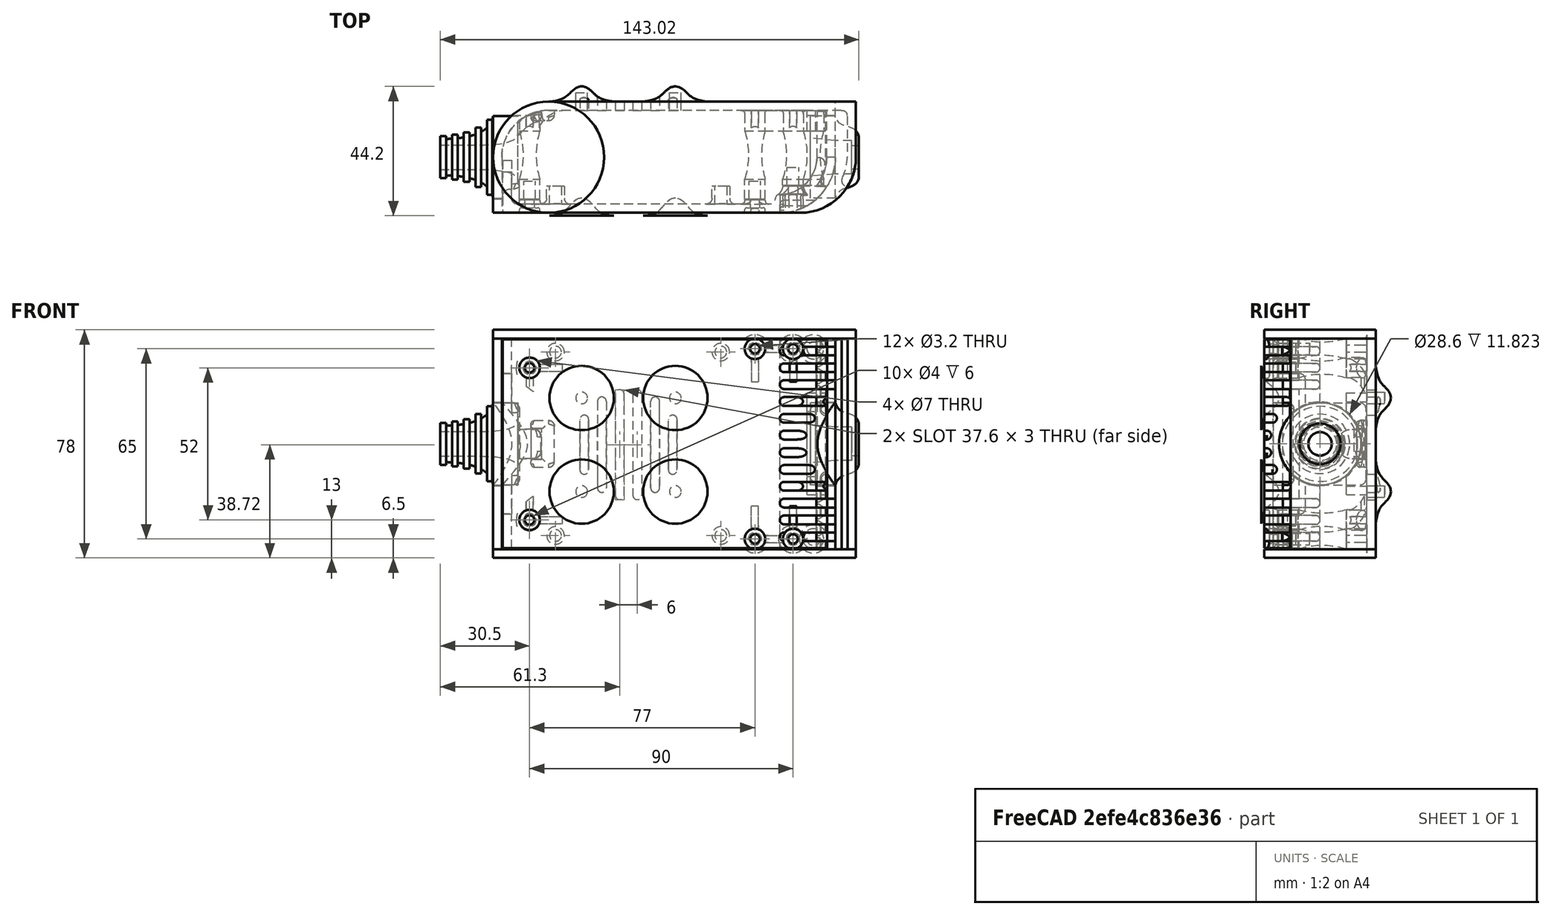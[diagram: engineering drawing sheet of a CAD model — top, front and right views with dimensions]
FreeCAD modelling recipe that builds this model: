
FCSTD DOCUMENT  (FreeCAD 0.19R0.19.2)
Label: enclosure_129
License: All rights reserved
LicenseURL: http://en.wikipedia.org/wiki/All_rights_reserved
objects: Part::Feature×74, Part::Revolution×74, Part::MultiFuse×61, Sketcher::SketchObject×38, Part::Fillet×27, Part::Extrusion×26, Part::Cut×25, Part::Cylinder×22, Part::Box×12, App::MeasureDistance×4
note: 359 computed .brp shape members not serialized (recipe doc carries the construction recipe); baked Part::Feature solids carry a one-line shape summary decoded from their .brp

FEATURE [Sketcher::SketchObject] Sketch  label="topSketch"
  FullyConstrained = true
  sketch-geometry (20):
    g0: LineSegment StartX=5.21097e-06 StartY=3 StartZ=0 EndX=5.21097e-06 EndY=19 EndZ=0
    g1: ArcOfCircle CenterX=19 CenterY=19 CenterZ=0 NormalX=0 NormalY=0 NormalZ=1 AngleXU=0 Radius=19 StartAngle=1.5708 EndAngle=3.14159
    g2: ArcOfCircle CenterX=19 CenterY=19 CenterZ=0 NormalX=0 NormalY=0 NormalZ=1 AngleXU=0 Radius=16 StartAngle=1.5708 EndAngle=3.14159
    g3: LineSegment StartX=114 StartY=35 StartZ=0 EndX=19 EndY=35 EndZ=0
    g4: LineSegment StartX=5.21097e-06 StartY=3 StartZ=0 EndX=5.21097e-06 EndY=0 EndZ=0
    g5: LineSegment StartX=3 StartY=0 StartZ=0 EndX=5.21097e-06 EndY=0 EndZ=0
    g6: LineSegment StartX=3 StartY=19 StartZ=0 EndX=3 EndY=0 EndZ=0
    g7: LineSegment StartX=19 StartY=38 StartZ=0 EndX=124 EndY=38 EndZ=0
    g8: Circle CenterX=119 CenterY=35 CenterZ=0 NormalX=0 NormalY=0 NormalZ=1 AngleXU=0 Radius=1
    g9: Circle CenterX=121 CenterY=35 CenterZ=0 NormalX=0 NormalY=0 NormalZ=1 AngleXU=0 Radius=1
    g10: Circle CenterX=121 CenterY=33 CenterZ=0 NormalX=0 NormalY=0 NormalZ=1 AngleXU=0 Radius=1
    g11: BSplineCurve PolesCount=3 KnotsCount=2 Degree=2 IsPeriodic=0
    g12: GeomPoint X=119 Y=35 Z=0
    g13: GeomPoint X=121 Y=33 Z=0
    g14: LineSegment StartX=119 StartY=35 StartZ=0 EndX=114 EndY=35 EndZ=0
    g15: ArcOfCircle CenterX=105 CenterY=19 CenterZ=0 NormalX=0 NormalY=0 NormalZ=1 AngleXU=0 Radius=19 StartAngle=5.7297 EndAngle=6.28319
    g16: ArcOfCircle CenterX=105 CenterY=19 CenterZ=0 NormalX=0 NormalY=0 NormalZ=1 AngleXU=0 Radius=16 StartAngle=5.60905 EndAngle=6.28319
    g17: LineSegment StartX=121 StartY=33 StartZ=0 EndX=121 EndY=19 EndZ=0
    g18: LineSegment StartX=124 StartY=38 StartZ=0 EndX=124 EndY=19 EndZ=0
    g19: LineSegment StartX=117.5 StartY=9.01251 StartZ=0 EndX=121.163 EndY=9.0125 EndZ=0
  constraints (46):
    c: Vertical(g0)
    c: Block(g0)
    c: Coincident(g1,g0)
    c: Block(g1)
    c: Coincident(g2,g1)
    c: Block(g2)
    c: Coincident(g3,g2)
    c: Horizontal(g3)
    c: Tangent(g3,g2)
    c: Coincident(g4,g0)
    c: Distance(g4) = 3
    c: Vertical(g4)
    c: Coincident(g5,g4)
    c: Horizontal(g5)
    c: Coincident(g6,g2)
    c: Coincident(g6,g5)
    c: Vertical(g6)
    c: Horizontal(g7)
    c: Distance(g7) = 105
    c: Coincident(g7,g1)
    c: Block(g3)
    c: Weight(g8) = 1
    c: Equal(g8,g9)
    c: Equal(g8,g10)
    c: InternalAlignment(g8,g11)
    c: InternalAlignment(g9,g11)
    c: InternalAlignment(g10,g11)
    c: InternalAlignment(g12,g11)
    c: InternalAlignment(g13,g11)
    c: Block(g11)
    c: Coincident(g14,g11)
    c: Coincident(g14,g3)
    c: Horizontal(g14)
    c: Block(g15)
    c: Coincident(g16,g15)
    c: Block(g16)
    c: Coincident(g17,g11)
    c: Coincident(g17,g16)
    c: Vertical(g17)
    c: Distance(g17) = 14
    c: Coincident(g18,g7)
    c: Coincident(g18,g15)
    c: Vertical(g18)
    c: Distance(g18) = 19
    c: Coincident(g19,g16)
    c: Coincident(g19,g15)
FEATURE [Sketcher::SketchObject] Sketch001  label="bottomSketch"
  FullyConstrained = true
  sketch-geometry (32):
    g0: LineSegment StartX=3.3 StartY=-6.03275e-07 StartZ=0 EndX=98 EndY=-6.03275e-07 EndZ=0
    g1: ArcOfCircle CenterX=98 CenterY=19 CenterZ=0 NormalX=0 NormalY=0 NormalZ=1 AngleXU=0 Radius=19 StartAngle=4.71239 EndAngle=5.71103
    g2: LineSegment StartX=6.3 StartY=8 StartZ=0 EndX=3.3 EndY=8 EndZ=0
    g3: LineSegment StartX=3.3 StartY=8 StartZ=0 EndX=3.3 EndY=-6.03275e-07 EndZ=0
    g4: ArcOfCircle CenterX=8.3 CenterY=5 CenterZ=0 NormalX=0 NormalY=0 NormalZ=1 AngleXU=0 Radius=2 StartAngle=3.14159 EndAngle=4.71239
    g5: LineSegment StartX=6.3 StartY=8 StartZ=0 EndX=6.3 EndY=5 EndZ=0
    g6: ArcOfCircle CenterX=98 CenterY=19 CenterZ=0 NormalX=0 NormalY=0 NormalZ=1 AngleXU=0 Radius=12.7 StartAngle=4.71239 EndAngle=6.28319
    g7: LineSegment StartX=94.7 StartY=3 StartZ=0 EndX=8.3 EndY=3 EndZ=0
    g8-g12: Circle x5 (B-spline internal-alignment scaffolding for g13; pole/knot coordinates omitted)
    g13: BSplineCurve PolesCount=5 KnotsCount=3 Degree=3 IsPeriodic=0
    g14: GeomPoint X=98 Y=6.3 Z=0
    g15: GeomPoint X=96.3938 Y=4.71946 Z=0
    g16: GeomPoint X=94.7 Y=3 Z=0
    g17-g23: Circle x7 (B-spline internal-alignment scaffolding for g24; pole/knot coordinates omitted)
    g24: BSplineCurve PolesCount=7 KnotsCount=5 Degree=3 IsPeriodic=0
    g25-g29: GeomPoint x5 (B-spline internal-alignment scaffolding for g24; pole/knot coordinates omitted)
    g30: ArcOfCircle CenterX=98 CenterY=19 CenterZ=0 NormalX=0 NormalY=0 NormalZ=1 AngleXU=0 Radius=15.7 StartAngle=5.81226 EndAngle=6.28319
    g31: LineSegment StartX=110.7 StartY=19 StartZ=0 EndX=113.7 EndY=19 EndZ=0
  constraints (41):
    c: Horizontal(g0)
    c: Coincident(g1,g0)
    c: Block(g1)
    c: Horizontal(g2)
    c: Distance(g2) = 3
    c: Coincident(g3,g2)
    c: Vertical(g3)
    c: Coincident(g3,g0)
    c: Block(g4)
    c: Block(g2)
    c: Coincident(g5,g2)
    c: Coincident(g5,g4)
    c: Vertical(g5)
    c: Coincident(g6,g1)
    c: Block(g6)
    c: Coincident(g7,g4)
    c: Horizontal(g7)
    c: Block(g0)
    c: Block(g7)
    c: Block(g3)
    c: Coincident(g13,g6)
    c: Weight(g8) = 1
    c: Equal(g8, g9-g12) x4
    c: Coincident(g13,g7)
    c: InternalAlignment(g8-g12 -> g13) x5
    c: InternalAlignment(g14,g13)
    c: InternalAlignment(g15,g13)
    c: InternalAlignment(g16,g13)
    c: Block(g13)
    c: Weight(g17) = 1
    c: Equal(g17, g18-g23) x6
    c: Coincident(g24,g1)
    c: InternalAlignment(g17-g23 -> g24) x7
    c: InternalAlignment(g25-g29 -> g24) x5
    c: Block(g24)
    c: Coincident(g30,g24)
    c: Coincident(g31,g6)
    c: Coincident(g31,g30)
    c: Horizontal(g31)
    c: Block(g31)
    c: Block(g30)
FEATURE [Part::Extrusion] Extrude  label="top"
  Base = -> Sketch
  Dir = (0,0,1)
  DirMode = 2
  FaceMakerClass = Part::FaceMakerBullseye
  LengthFwd = 72
  LengthRev = 0
  Solid = true
  Symmetric = false
FEATURE [Part::Extrusion] Extrude001  label="bottom"
  Base = -> Sketch001
  Dir = (0,0,1)
  DirMode = 2
  FaceMakerClass = Part::FaceMakerBullseye
  LengthFwd = 71.4
  LengthRev = 0
  Placement = pos=(0,0,0.3) rot=(0,0,1;0rad)
  Solid = true
  Symmetric = false
FEATURE [Sketcher::SketchObject] Sketch002  label="topSketch001"
  FullyConstrained = true
  sketch-geometry (6):
    g0: ArcOfCircle CenterX=19 CenterY=19 CenterZ=0 NormalX=0 NormalY=0 NormalZ=1 AngleXU=0 Radius=19 StartAngle=1.5708 EndAngle=3.14159
    g1: LineSegment StartX=5.22862e-06 StartY=19 StartZ=0 EndX=5.22862e-06 EndY=1.19904e-11 EndZ=0
    g2: LineSegment StartX=19 StartY=38 StartZ=0 EndX=124 EndY=38 EndZ=0
    g3: LineSegment StartX=5.22862e-06 StartY=1.19904e-11 StartZ=0 EndX=105 EndY=1.19904e-11 EndZ=0
    g4: ArcOfCircle CenterX=105 CenterY=19 CenterZ=0 NormalX=0 NormalY=0 NormalZ=1 AngleXU=0 Radius=19 StartAngle=4.71239 EndAngle=6.28319
    g5: LineSegment StartX=124 StartY=38 StartZ=0 EndX=124 EndY=19 EndZ=0
  constraints (16):
    c: Block(g0)
    c: Coincident(g1,g0)
    c: Vertical(g1)
    c: Horizontal(g2)
    c: Distance(g2) = 105
    c: Coincident(g2,g0)
    c: Distance(g1) = 19
    c: Coincident(g3,g1)
    c: Horizontal(g3)
    c: Distance(g3) = 105
    c: Block(g4)
    c: Coincident(g4,g3)
    c: Coincident(g5,g2)
    c: Coincident(g5,g4)
    c: Vertical(g5)
    c: Distance(g5) = 19
FEATURE [Part::Extrusion] Extrude002  label="sideA"
  Base = -> Sketch002
  Dir = (0,0,1)
  DirMode = 2
  FaceMakerClass = Part::FaceMakerBullseye
  LengthFwd = 3
  LengthRev = 0
  Placement = pos=(0,0,-3) rot=(0,0,1;0rad)
  Solid = true
  Symmetric = false
FEATURE [Sketcher::SketchObject] Sketch003  label="topSketch002"
  FullyConstrained = true
  sketch-geometry (6):
    g0: LineSegment StartX=19 StartY=38 StartZ=0 EndX=117 EndY=38 EndZ=0
    g1: ArcOfCircle CenterX=19 CenterY=19 CenterZ=0 NormalX=0 NormalY=0 NormalZ=1 AngleXU=0 Radius=19 StartAngle=1.5708 EndAngle=3.14159
    g2: LineSegment StartX=117 StartY=38 StartZ=0 EndX=117 EndY=19 EndZ=0
    g3: LineSegment StartX=98 StartY=1.0161e-12 StartZ=0 EndX=5.22862e-06 EndY=1.0161e-12 EndZ=0
    g4: LineSegment StartX=5.22862e-06 StartY=19 StartZ=0 EndX=5.22862e-06 EndY=1.0161e-12 EndZ=0
    g5: ArcOfCircle CenterX=98 CenterY=19 CenterZ=0 NormalX=0 NormalY=0 NormalZ=1 AngleXU=0 Radius=19 StartAngle=4.71239 EndAngle=6.28319
  constraints (16):
    c: Horizontal(g0)
    c: Distance(g0) = 98
    c: Coincident(g1,g0)
    c: Block(g1)
    c: Coincident(g2,g0)
    c: Vertical(g2)
    c: Distance(g2) = 19
    c: Horizontal(g3)
    c: Coincident(g4,g1)
    c: Vertical(g4)
    c: Coincident(g3,g4)
    c: Block(g3)
    c: Coincident(g5,g2)
    c: Coincident(g5,g3)
    c: Block(g0)
    c: Block(g5)
FEATURE [Sketcher::SketchObject] Sketch004
  FullyConstrained = true
  MapMode = 3
  Placement = pos=(0,0,0) rot=(1,0,0;1.5708rad)
  Support = -> [Extrude]
  sketch-geometry (8):
    g0: Circle CenterX=80.351 CenterY=-67.6202 CenterZ=0 NormalX=0 NormalY=0 NormalZ=1 AngleXU=0 Radius=2
    g1: Circle CenterX=80.351 CenterY=-67.6202 CenterZ=0 NormalX=0 NormalY=0 NormalZ=1 AngleXU=0 Radius=3
    g2: Circle CenterX=80.351 CenterY=-4.92017 CenterZ=0 NormalX=0 NormalY=0 NormalZ=1 AngleXU=0 Radius=2
    g3: Circle CenterX=80.351 CenterY=-4.92017 CenterZ=0 NormalX=0 NormalY=0 NormalZ=1 AngleXU=0 Radius=3
    g4: Circle CenterX=23.851 CenterY=-4.92017 CenterZ=0 NormalX=0 NormalY=0 NormalZ=1 AngleXU=0 Radius=2
    g5: Circle CenterX=23.851 CenterY=-4.92017 CenterZ=0 NormalX=0 NormalY=0 NormalZ=1 AngleXU=0 Radius=3
    g6: Circle CenterX=23.851 CenterY=-67.6202 CenterZ=0 NormalX=0 NormalY=0 NormalZ=1 AngleXU=0 Radius=2
    g7: Circle CenterX=23.851 CenterY=-67.6202 CenterZ=0 NormalX=0 NormalY=0 NormalZ=1 AngleXU=0 Radius=3
  constraints (8):
    c: Block(g3)
    c: Block(g2)
    c: Block(g1)
    c: Block(g0)
    c: Block(g6)
    c: Block(g7)
    c: Block(g4)
    c: Block(g5)
FEATURE [Part::Extrusion] Extrude004
  Base = -> Sketch004
  Dir = (0,-1,2e-16)
  DirMode = 2
  FaceMakerClass = Part::FaceMakerBullseye
  LengthFwd = 6
  LengthRev = 0
  Placement = pos=(0,9,0) rot=(0,0,1;0rad)
  Solid = true
  Symmetric = false
FEATURE [Sketcher::SketchObject] Sketch005
  FullyConstrained = true
  MapMode = 3
  Placement = pos=(0,0,0) rot=(1,0,0;1.5708rad)
  Support = -> [Extrude]
  sketch-geometry (8):
    g0: Circle CenterX=80.351 CenterY=-67.6202 CenterZ=0 NormalX=0 NormalY=0 NormalZ=1 AngleXU=0 Radius=3
    g1: Circle CenterX=80.351 CenterY=-4.92017 CenterZ=0 NormalX=0 NormalY=0 NormalZ=1 AngleXU=0 Radius=3
    g2: Circle CenterX=23.851 CenterY=-4.92017 CenterZ=0 NormalX=0 NormalY=0 NormalZ=1 AngleXU=0 Radius=3
    g3: Circle CenterX=23.851 CenterY=-67.6202 CenterZ=0 NormalX=0 NormalY=0 NormalZ=1 AngleXU=0 Radius=3
    g4: Circle CenterX=23.851 CenterY=-67.6202 CenterZ=0 NormalX=0 NormalY=0 NormalZ=1 AngleXU=0 Radius=5
    g5: Circle CenterX=80.351 CenterY=-67.6202 CenterZ=0 NormalX=0 NormalY=0 NormalZ=1 AngleXU=0 Radius=5
    g6: Circle CenterX=23.851 CenterY=-4.92017 CenterZ=0 NormalX=0 NormalY=0 NormalZ=1 AngleXU=0 Radius=5
    g7: Circle CenterX=80.351 CenterY=-4.92017 CenterZ=0 NormalX=0 NormalY=0 NormalZ=1 AngleXU=0 Radius=5
  constraints (8):
    c: Block(g1)
    c: Block(g0)
    c: Block(g3)
    c: Block(g2)
    c: Block(g5)
    c: Block(g4)
    c: Block(g6)
    c: Block(g7)
FEATURE [Part::Extrusion] Extrude005
  Base = -> Sketch005
  Dir = (0,-1,2e-16)
  DirMode = 2
  FaceMakerClass = Part::FaceMakerBullseye
  LengthFwd = 2
  LengthRev = 0
  Solid = true
  Symmetric = false
FEATURE [Sketcher::SketchObject] Sketch006
  FullyConstrained = true
  MapMode = 3
  Placement = pos=(0,0,0) rot=(1,0,0;1.5708rad)
  sketch-geometry (8):
    g0: Circle CenterX=80.351 CenterY=-67.6202 CenterZ=0 NormalX=0 NormalY=0 NormalZ=1 AngleXU=0 Radius=3
    g1: Circle CenterX=80.351 CenterY=-4.92017 CenterZ=0 NormalX=0 NormalY=0 NormalZ=1 AngleXU=0 Radius=3
    g2: Circle CenterX=23.851 CenterY=-4.92017 CenterZ=0 NormalX=0 NormalY=0 NormalZ=1 AngleXU=0 Radius=3
    g3: Circle CenterX=23.851 CenterY=-67.6202 CenterZ=0 NormalX=0 NormalY=0 NormalZ=1 AngleXU=0 Radius=3
    g4: Circle CenterX=23.851 CenterY=-67.6202 CenterZ=0 NormalX=0 NormalY=0 NormalZ=1 AngleXU=0 Radius=5
    g5: Circle CenterX=80.351 CenterY=-67.6202 CenterZ=0 NormalX=0 NormalY=0 NormalZ=1 AngleXU=0 Radius=5
    g6: Circle CenterX=23.851 CenterY=-4.92017 CenterZ=0 NormalX=0 NormalY=0 NormalZ=1 AngleXU=0 Radius=5
    g7: Circle CenterX=80.351 CenterY=-4.92017 CenterZ=0 NormalX=0 NormalY=0 NormalZ=1 AngleXU=0 Radius=5
  constraints (8):
    c: Block(g1)
    c: Block(g0)
    c: Block(g3)
    c: Block(g2)
    c: Block(g5)
    c: Block(g4)
    c: Block(g6)
    c: Block(g7)
FEATURE [Part::Extrusion] Extrude007
  Base = -> Sketch006
  Dir = (0,-1,2e-16)
  DirMode = 2
  FaceMakerClass = Part::FaceMakerBullseye
  LengthFwd = 2
  LengthRev = 0
  Solid = true
  Symmetric = false
FEATURE [Part::Fillet] Fillet
  Base = -> Extrude007
  Edges = 4 edges r=1.99: [Edge6,Edge12,Edge18,Edge24]
FEATURE [Part::Cut] Cut
  Base = -> Extrude005
  Placement = pos=(0,5,0) rot=(0,0,1;0rad)
  Tool = -> Fillet
FEATURE [Part::MultiFuse] Fusion  label="pCBScrews"
  Placement = pos=(-2.5,0,72.3) rot=(0,0,1;0rad)
  Shapes = -> [Extrude004,Cut]
FEATURE [App::MeasureDistance] Distance  label="Distance: 0.69 mm"
  Distance = 0.685967
  P1 = (24.0138,2.9647,0.3)
  P2 = (23.8901,3,-0.373787)
FEATURE [App::MeasureDistance] Distance001  label="Distance: 0.53 mm"
  Distance = 0.533607
  P1 = (80.2939,3,72.2334)
  P2 = (80.281,2.99661,71.7)
FEATURE [Part::Fillet] Fillet001
  Base = -> Extrude001
  Edges = 1 edges r=2.4: [Edge17]
FEATURE [Part::Fillet] Fillet002  label="bottom001"
  Base = -> Fillet001
  Edges = 1 edges r=2.4: [Edge36]
FEATURE [Part::Fillet] Fillet003  label="top001"
  Base = -> Extrude
  Edges = 1 edges r=2: [Edge1]
FEATURE [Sketcher::SketchObject] Sketch007
  FullyConstrained = true
  sketch-geometry (16):
    g0: LineSegment StartX=4 StartY=0 StartZ=0 EndX=4 EndY=2.4 EndZ=0
    g1: LineSegment StartX=4 StartY=2.4 StartZ=0 EndX=7 EndY=2.4 EndZ=0
    g2: LineSegment StartX=4 StartY=0 StartZ=0 EndX=5.7 EndY=0 EndZ=0
    g3: LineSegment StartX=5.7 StartY=0 StartZ=0 EndX=5.7 EndY=-5.6 EndZ=0
    g4-g8: Circle x5 (B-spline internal-alignment scaffolding for g9; pole/knot coordinates omitted)
    g9: BSplineCurve PolesCount=5 KnotsCount=3 Degree=3 IsPeriodic=0
    g10: GeomPoint X=7 Y=2.4 Z=0
    g11: GeomPoint X=10.4582 Y=-1.55472 Z=0
    g12: GeomPoint X=14 Y=-5.6 Z=0
    g13: LineSegment StartX=14 StartY=-5.6 StartZ=0 EndX=14 EndY=-14.1 EndZ=0
    g14: LineSegment StartX=14 StartY=-14.1 StartZ=0 EndX=6.5 EndY=-14.1 EndZ=0
    g15: LineSegment StartX=5.7 StartY=-5.6 StartZ=0 EndX=6.5 EndY=-14.1 EndZ=0
  constraints (28):
    c: Distance(g0) = 2.4
    c: Vertical(g0)
    c: Block(g0)
    c: Coincident(g1,g0)
    c: Horizontal(g1)
    c: Distance(g1) = 3
    c: Coincident(g2,g0)
    c: Horizontal(g2)
    c: Distance(g2) = 1.7
    c: Coincident(g3,g2)
    c: Vertical(g3)
    c: Distance(g3) = 5.6
    c: Coincident(g9,g1)
    c: Weight(g4) = 1
    c: Equal(g4, g5-g8) x4
    c: InternalAlignment(g4-g8 -> g9) x5
    c: InternalAlignment(g10,g9)
    c: InternalAlignment(g11,g9)
    c: InternalAlignment(g12,g9)
    c: Block(g9)
    c: Coincident(g13,g9)
    c: Vertical(g13)
    c: Distance(g13) = 8.5
    c: Coincident(g14,g13)
    c: Horizontal(g14)
    c: Distance(g14) = 7.5
    c: Coincident(g15,g3)
    c: Coincident(g15,g14)
FEATURE [Part::Feature] Face
  shape: bbox 10 x 16.5 x 2e-07 mm, 1 faces, 0 solids (baked)
FEATURE [Part::Revolution] Revolve  label="plugHousing"
  Angle = 360
  Axis = (0,1,0)
  Base = (0,0,0)
  FaceMakerClass = Part::FaceMakerBullseye
  Placement = pos=(0,0,36.15) rot=(0,0,1;0rad)
  Solid = false
  Source = -> Face
  Symmetric = false
FEATURE [Part::Feature] Face001
  shape: bbox 10 x 16.5 x 2e-07 mm, 1 faces, 0 solids (baked)
FEATURE [Part::Revolution] Revolve001  label="plugHousing001"
  Angle = 360
  Axis = (0,1,0)
  Base = (0,0,0)
  FaceMakerClass = Part::FaceMakerBullseye
  Placement = pos=(0,0,36.15) rot=(0,0,1;0rad)
  Solid = false
  Source = -> Face001
  Symmetric = false
FEATURE [Part::MultiFuse] Fusion001  label="plugHousing002"
  Placement = pos=(0,0,0) rot=(0,0,1;1.5708rad)
  Shapes = -> [Revolve001,Revolve]
FEATURE [Part::Feature] Face002
  shape: bbox 10 x 16.5 x 2e-07 mm, 1 faces, 0 solids (baked)
FEATURE [Part::Revolution] Revolve003  label="plugHousing005"
  Angle = 360
  Axis = (0,1,0)
  Base = (0,0,0)
  FaceMakerClass = Part::FaceMakerBullseye
  Placement = pos=(0,0,36.15) rot=(0,0,1;0rad)
  Solid = false
  Source = -> Face002
  Symmetric = false
FEATURE [Part::Feature] Face003
  shape: bbox 10 x 16.5 x 2e-07 mm, 1 faces, 0 solids (baked)
FEATURE [Part::Revolution] Revolve002  label="plugHousing003"
  Angle = 360
  Axis = (0,1,0)
  Base = (0,0,0)
  FaceMakerClass = Part::FaceMakerBullseye
  Placement = pos=(0,0,36.15) rot=(0,0,1;0rad)
  Solid = false
  Source = -> Face003
  Symmetric = false
FEATURE [Part::MultiFuse] Fusion002  label="plugHousing004"
  Placement = pos=(0,0,0) rot=(0,0,1;1.5708rad)
  Shapes = -> [Revolve002,Revolve003]
FEATURE [Part::MultiFuse] Fusion003  label="plugHousing006"
  Placement = pos=(0,19,0) rot=(0,0,1;3.14159rad)
  Shapes = -> [Fusion002,Fusion001]
FEATURE [Part::Feature] Face004
  shape: bbox 10 x 16.5 x 2e-07 mm, 1 faces, 0 solids (baked)
FEATURE [Part::Revolution] Revolve006  label="plugHousing010"
  Angle = 360
  Axis = (0,1,0)
  Base = (0,0,0)
  FaceMakerClass = Part::FaceMakerBullseye
  Placement = pos=(0,0,36.15) rot=(0,0,1;0rad)
  Solid = false
  Source = -> Face004
  Symmetric = false
FEATURE [Part::Feature] Face005
  shape: bbox 10 x 16.5 x 2e-07 mm, 1 faces, 0 solids (baked)
FEATURE [Part::Revolution] Revolve007  label="plugHousing011"
  Angle = 360
  Axis = (0,1,0)
  Base = (0,0,0)
  FaceMakerClass = Part::FaceMakerBullseye
  Placement = pos=(0,0,36.15) rot=(0,0,1;0rad)
  Solid = false
  Source = -> Face005
  Symmetric = false
FEATURE [Part::Feature] Face006
  shape: bbox 10 x 16.5 x 2e-07 mm, 1 faces, 0 solids (baked)
FEATURE [Part::Revolution] Revolve004  label="plugHousing007"
  Angle = 360
  Axis = (0,1,0)
  Base = (0,0,0)
  FaceMakerClass = Part::FaceMakerBullseye
  Placement = pos=(0,0,36.15) rot=(0,0,1;0rad)
  Solid = false
  Source = -> Face006
  Symmetric = false
FEATURE [Part::MultiFuse] Fusion004  label="plugHousing009"
  Placement = pos=(0,0,0) rot=(0,0,1;1.5708rad)
  Shapes = -> [Revolve004,Revolve007]
FEATURE [Part::Feature] Face007
  shape: bbox 10 x 16.5 x 2e-07 mm, 1 faces, 0 solids (baked)
FEATURE [Part::Revolution] Revolve005  label="plugHousing008"
  Angle = 360
  Axis = (0,1,0)
  Base = (0,0,0)
  FaceMakerClass = Part::FaceMakerBullseye
  Placement = pos=(0,0,36.15) rot=(0,0,1;0rad)
  Solid = false
  Source = -> Face007
  Symmetric = false
FEATURE [Part::MultiFuse] Fusion005  label="plugHousing012"
  Placement = pos=(0,0,0) rot=(0,0,1;1.5708rad)
  Shapes = -> [Revolve006,Revolve005]
FEATURE [Part::MultiFuse] Fusion006  label="plugHousing013"
  Placement = pos=(0,19,0) rot=(0,0,1;3.14159rad)
  Shapes = -> [Fusion005,Fusion004]
FEATURE [Part::MultiFuse] Fusion007  label="plugHousing014"
  Placement = pos=(122.621,0,-0.15) rot=(0,0,1;0rad)
  Shapes = -> [Fusion003,Fusion006]
FEATURE [Part::Cylinder] Cylinder002
  Angle = 360
  AttacherType = Attacher::AttachEngine3D
  Height = 20
  Placement = pos=(0,0,36.15) rot=(0,0,1;0rad)
  Radius = 4
FEATURE [Part::Cylinder] Cylinder003
  Angle = 360
  AttacherType = Attacher::AttachEngine3D
  Height = 10
  Placement = pos=(0,0,36.15) rot=(0,0,1;0rad)
  Radius = 4
FEATURE [Part::MultiFuse] Fusion009  label="removeToCreateHoleForPlugHousing"
  Placement = pos=(70,19,36.15) rot=(0,1,0;1.5708rad)
  Shapes = -> [Cylinder002,Cylinder003]
FEATURE [Part::Cylinder] Cylinder004
  Angle = 360
  AttacherType = Attacher::AttachEngine3D
  Height = 20
  Placement = pos=(0,0,36.15) rot=(0,0,1;0rad)
  Radius = 4
FEATURE [Part::Cylinder] Cylinder005
  Angle = 360
  AttacherType = Attacher::AttachEngine3D
  Height = 10
  Placement = pos=(0,0,36.15) rot=(0,0,1;0rad)
  Radius = 4
FEATURE [Part::MultiFuse] Fusion010  label="removeToCreateHoleForPlugHousing001"
  Placement = pos=(70,19,36.15) rot=(0,1,0;1.5708rad)
  Shapes = -> [Cylinder004,Cylinder005]
FEATURE [Part::Cut] Cut001
  Base = -> Fillet003
  Tool = -> Fusion010
FEATURE [Part::Cut] Cut002  label="Bottom"
  Base = -> Fillet002
  Tool = -> Fusion009
FEATURE [Part::Feature] Face008
  shape: bbox 10 x 16.5 x 2e-07 mm, 1 faces, 0 solids (baked)
FEATURE [Part::Revolution] Revolve011  label="plugHousing021"
  Angle = 360
  Axis = (0,1,0)
  Base = (0,0,0)
  FaceMakerClass = Part::FaceMakerBullseye
  Placement = pos=(0,0,36.15) rot=(0,0,1;0rad)
  Solid = false
  Source = -> Face008
  Symmetric = false
FEATURE [Part::Feature] Face009
  shape: bbox 10 x 16.5 x 2e-07 mm, 1 faces, 0 solids (baked)
FEATURE [Part::Revolution] Revolve012  label="plugHousing022"
  Angle = 360
  Axis = (0,1,0)
  Base = (0,0,0)
  FaceMakerClass = Part::FaceMakerBullseye
  Placement = pos=(0,0,36.15) rot=(0,0,1;0rad)
  Solid = false
  Source = -> Face009
  Symmetric = false
FEATURE [Part::Feature] Face010 .. Face013  x4 (patterned run collapsed; names and placements below)
  shape: bbox 10 x 16.5 x 2e-07 mm, 1 faces, 0 solids (baked)
FEATURE [Part::Revolution] Revolve015  label="plugHousing027"
  Angle = 360
  Axis = (0,1,0)
  Base = (0,0,0)
  FaceMakerClass = Part::FaceMakerBullseye
  Placement = pos=(0,0,36.15) rot=(0,0,1;0rad)
  Solid = false
  Source = -> Face013
  Symmetric = false
FEATURE [Part::Feature] Face014
  shape: bbox 10 x 16.5 x 2e-07 mm, 1 faces, 0 solids (baked)
FEATURE [Part::Feature] Face015
  shape: bbox 10 x 16.5 x 2e-07 mm, 1 faces, 0 solids (baked)
FEATURE [Part::Feature] Face016
  shape: bbox 10 x 16.5 x 2e-07 mm, 1 faces, 0 solids (baked)
FEATURE [Part::Revolution] Revolve019  label="plugHousing033"
  Angle = 360
  Axis = (0,1,0)
  Base = (0,0,0)
  FaceMakerClass = Part::FaceMakerBullseye
  Placement = pos=(0,0,36.15) rot=(0,0,1;0rad)
  Solid = false
  Source = -> Face016
  Symmetric = false
FEATURE [Part::Feature] Face017
  shape: bbox 10 x 16.5 x 2e-07 mm, 1 faces, 0 solids (baked)
FEATURE [Part::Revolution] Revolve020  label="plugHousing034"
  Angle = 360
  Axis = (0,1,0)
  Base = (0,0,0)
  FaceMakerClass = Part::FaceMakerBullseye
  Placement = pos=(0,0,36.15) rot=(0,0,1;0rad)
  Solid = false
  Source = -> Face017
  Symmetric = false
FEATURE [Part::Feature] Face018
  shape: bbox 10 x 16.5 x 2e-07 mm, 1 faces, 0 solids (baked)
FEATURE [Part::Revolution] Revolve016  label="plugHousing030"
  Angle = 360
  Axis = (0,1,0)
  Base = (0,0,0)
  FaceMakerClass = Part::FaceMakerBullseye
  Placement = pos=(0,0,36.15) rot=(0,0,1;0rad)
  Solid = false
  Source = -> Face018
  Symmetric = false
FEATURE [Part::MultiFuse] Fusion020  label="plugHousing038"
  Placement = pos=(0,0,0) rot=(0,0,1;1.5708rad)
  Shapes = -> [Revolve016,Revolve020]
FEATURE [Part::Feature] Face019
  shape: bbox 10 x 16.5 x 2e-07 mm, 1 faces, 0 solids (baked)
FEATURE [Part::Feature] Face020
  shape: bbox 10 x 16.5 x 2e-07 mm, 1 faces, 0 solids (baked)
FEATURE [Part::Revolution] Revolve017  label="plugHousing031"
  Angle = 360
  Axis = (0,1,0)
  Base = (0,0,0)
  FaceMakerClass = Part::FaceMakerBullseye
  Placement = pos=(0,0,36.15) rot=(0,0,1;0rad)
  Solid = false
  Source = -> Face020
  Symmetric = false
FEATURE [Part::MultiFuse] Fusion021  label="plugHousing039"
  Placement = pos=(0,0,0) rot=(0,0,1;1.5708rad)
  Shapes = -> [Revolve019,Revolve017]
FEATURE [Part::MultiFuse] Fusion023  label="plugHousing041"
  Placement = pos=(0,19,0) rot=(0,0,1;3.14159rad)
  Shapes = -> [Fusion021,Fusion020]
FEATURE [Part::Revolution] Revolve022  label="plugHousing043"
  Angle = 360
  Axis = (0,1,0)
  Base = (0,0,0)
  FaceMakerClass = Part::FaceMakerBullseye
  Placement = pos=(0,0,36.15) rot=(0,0,1;0rad)
  Solid = false
  Source = -> Face019
  Symmetric = false
FEATURE [Part::Feature] Face021
  shape: bbox 10 x 16.5 x 2e-07 mm, 1 faces, 0 solids (baked)
FEATURE [Part::Revolution] Revolve023  label="plugHousing044"
  Angle = 360
  Axis = (0,1,0)
  Base = (0,0,0)
  FaceMakerClass = Part::FaceMakerBullseye
  Placement = pos=(0,0,36.15) rot=(0,0,1;0rad)
  Solid = false
  Source = -> Face021
  Symmetric = false
FEATURE [Part::Feature] Face022
  shape: bbox 10 x 16.5 x 2e-07 mm, 1 faces, 0 solids (baked)
FEATURE [Part::Revolution] Revolve018  label="plugHousing032"
  Angle = 360
  Axis = (0,1,0)
  Base = (0,0,0)
  FaceMakerClass = Part::FaceMakerBullseye
  Placement = pos=(0,0,36.15) rot=(0,0,1;0rad)
  Solid = false
  Source = -> Face022
  Symmetric = false
FEATURE [Part::MultiFuse] Fusion022  label="plugHousing040"
  Placement = pos=(0,0,0) rot=(0,0,1;1.5708rad)
  Shapes = -> [Revolve018,Revolve023]
FEATURE [Part::Feature] Face023
  shape: bbox 10 x 16.5 x 2e-07 mm, 1 faces, 0 solids (baked)
FEATURE [Part::Revolution] Revolve021  label="plugHousing035"
  Angle = 360
  Axis = (0,1,0)
  Base = (0,0,0)
  FaceMakerClass = Part::FaceMakerBullseye
  Placement = pos=(0,0,36.15) rot=(0,0,1;0rad)
  Solid = false
  Source = -> Face023
  Symmetric = false
FEATURE [Part::MultiFuse] Fusion018  label="plugHousing036"
  Placement = pos=(0,0,0) rot=(0,0,1;1.5708rad)
  Shapes = -> [Revolve022,Revolve021]
FEATURE [Part::MultiFuse] Fusion019  label="plugHousing037"
  Placement = pos=(0,19,0) rot=(0,0,1;3.14159rad)
  Shapes = -> [Fusion018,Fusion022]
FEATURE [Part::MultiFuse] Fusion024  label="plugHousing042"
  Placement = pos=(122.621,0,-0.15) rot=(0,0,1;0rad)
  Shapes = -> [Fusion023,Fusion019]
FEATURE [Part::Cylinder] Cylinder006
  Angle = 360
  AttacherType = Attacher::AttachEngine3D
  Height = 20
  Placement = pos=(0,0,36.15) rot=(0,0,1;0rad)
  Radius = 14.3
FEATURE [Part::Cylinder] Cylinder007
  Angle = 360
  AttacherType = Attacher::AttachEngine3D
  Height = 10
  Placement = pos=(0,0,36.15) rot=(0,0,1;0rad)
  Radius = 4
FEATURE [Part::MultiFuse] Fusion026  label="removeToCreteHoleForPlugHousing"
  Placement = pos=(70,19,36) rot=(0,1,0;1.5708rad)
  Shapes = -> [Cylinder006,Cylinder007]
FEATURE [Part::Box] Box001  label="Cube001"
  AttacherType = Attacher::AttachEngine3D
  Height = 28
  Length = 3
  Placement = pos=(110.7,19,22) rot=(0,0,1;0rad)
  Width = 15.7
FEATURE [Part::Cut] Cut003  label="top002"
  Base = -> Cut001
  Tool = -> Fusion007
FEATURE [Part::Revolution] Revolve008  label="plugHousing015"
  Angle = 360
  Axis = (0,1,0)
  Base = (0,0,0)
  FaceMakerClass = Part::FaceMakerBullseye
  Placement = pos=(0,0,36.15) rot=(0,0,1;0rad)
  Solid = false
  Source = -> Face010
  Symmetric = false
FEATURE [Part::MultiFuse] Fusion013  label="plugHousing020"
  Placement = pos=(0,0,0) rot=(0,0,1;1.5708rad)
  Shapes = -> [Revolve008,Revolve012]
FEATURE [Part::Cut] Cut004  label="top003"
  Base = -> Cut003
  Placement = pos=(1,0,0) rot=(0,0,1;0rad)
  Tool = -> Fusion026
FEATURE [Part::Cylinder] Cylinder008
  Angle = 360
  AttacherType = Attacher::AttachEngine3D
  Height = 20
  Placement = pos=(0,0,36.15) rot=(0,0,1;0rad)
  Radius = 10.3
FEATURE [Part::Cylinder] Cylinder009
  Angle = 360
  AttacherType = Attacher::AttachEngine3D
  Height = 10
  Placement = pos=(0,0,36.15) rot=(0,0,1;0rad)
  Radius = 4
FEATURE [Part::MultiFuse] Fusion027  label="removeToCreteHoleForPlugHousing001"
  Placement = pos=(70,19,36) rot=(0,1,0;1.5708rad)
  Shapes = -> [Cylinder008,Cylinder009]
FEATURE [Part::Cut] Cut005  label="plugHousingTab"
  Base = -> Box001
  Tool = -> Fusion027
FEATURE [Part::MultiFuse] Fusion028  label="plugHousing045"
  Shapes = -> [Fusion024,Cut005]
FEATURE [Part::Box] Box002  label="Cube002"
  AttacherType = Attacher::AttachEngine3D
  Height = 28.8
  Length = 3
  Placement = pos=(107.3,28,21.6) rot=(0,0,1;0rad)
  Width = 7
FEATURE [Part::Box] Box003  label="Cube003"
  AttacherType = Attacher::AttachEngine3D
  Height = 3
  Length = 6.4
  Placement = pos=(107.3,28,18.6) rot=(0,0,1;0rad)
  Width = 7
FEATURE [Part::Box] Box004  label="Cube004"
  AttacherType = Attacher::AttachEngine3D
  Height = 3
  Length = 6.4
  Placement = pos=(107.3,28,50.4) rot=(0,0,1;0rad)
  Width = 7
FEATURE [Part::MultiFuse] Fusion029  label="plugHousingBracketHolder"
  Shapes = -> [Box004,Box002,Box003]
FEATURE [Part::Cylinder] Cylinder010
  Angle = 360
  AttacherType = Attacher::AttachEngine3D
  Height = 20
  Placement = pos=(0,0,36.15) rot=(0,0,1;0rad)
  Radius = 14.3
FEATURE [Part::Cylinder] Cylinder011
  Angle = 360
  AttacherType = Attacher::AttachEngine3D
  Height = 10
  Placement = pos=(0,0,36.15) rot=(0,0,1;0rad)
  Radius = 4
FEATURE [Part::MultiFuse] Fusion030  label="removeToCreteHoleForPlugHousing002"
  Placement = pos=(70,19,36) rot=(0,1,0;1.5708rad)
  Shapes = -> [Cylinder010,Cylinder011]
FEATURE [Part::Cut] Cut006  label="plugHousingBracketHolder001"
  Base = -> Fusion029
  Tool = -> Fusion030
FEATURE [Part::Cylinder] Cylinder012
  Angle = 360
  AttacherType = Attacher::AttachEngine3D
  Height = 20
  Placement = pos=(0,0,36.15) rot=(0,0,1;0rad)
  Radius = 7
FEATURE [Part::Cylinder] Cylinder013
  Angle = 360
  AttacherType = Attacher::AttachEngine3D
  Height = 10
  Placement = pos=(0,0,36.15) rot=(0,0,1;0rad)
  Radius = 4
FEATURE [Part::MultiFuse] Fusion032  label="removeToCreteHoleForPlugHousing003"
  Placement = pos=(70,19,36) rot=(0,1,0;1.5708rad)
  Shapes = -> [Cylinder012,Cylinder013]
FEATURE [Part::Cut] Cut007  label="bottom002"
  Base = -> Cut002
  Tool = -> Fusion032
FEATURE [Sketcher::SketchObject] Sketch008
  FullyConstrained = true
  sketch-geometry (54):
    g0: LineSegment StartX=-4.2 StartY=0 StartZ=0 EndX=-6.2 EndY=0 EndZ=0
    g1: LineSegment StartX=-14 StartY=-18 StartZ=0 EndX=-14 EndY=-26.5 EndZ=0
    g2: LineSegment StartX=-4.2 StartY=0 StartZ=0 EndX=-4.2 EndY=-13.4877 EndZ=0
    g3: Circle CenterX=-4.2 CenterY=-13.4877 CenterZ=0 NormalX=0 NormalY=0 NormalZ=1 AngleXU=0 Radius=1
    g4: Circle CenterX=-4.2 CenterY=-26.5 CenterZ=0 NormalX=0 NormalY=0 NormalZ=1 AngleXU=0 Radius=1
    g5: Circle CenterX=-8.2 CenterY=-26.5 CenterZ=0 NormalX=0 NormalY=0 NormalZ=1 AngleXU=0 Radius=1
    g6: BSplineCurve PolesCount=3 KnotsCount=2 Degree=2 IsPeriodic=0
    g7: GeomPoint X=-4.2 Y=-13.4877 Z=0
    g8: GeomPoint X=-8.2 Y=-26.5 Z=0
    g9: LineSegment StartX=-14 StartY=-26.5 StartZ=0 EndX=-8.2 EndY=-26.5 EndZ=0
    g10: LineSegment StartX=-10.15 StartY=-12 StartZ=0 EndX=-10.15 EndY=-14 EndZ=0
    g11: LineSegment StartX=-12.8401 StartY=-16 StartZ=0 EndX=-10.1571 EndY=-16 EndZ=0
    g12: LineSegment StartX=-10.15 StartY=-14 StartZ=0 EndX=-8.70761 EndY=-14 EndZ=0
    g13: LineSegment StartX=-12.8401 StartY=-16 StartZ=0 EndX=-12.8401 EndY=-17.6958 EndZ=0
    g14: LineSegment StartX=-10.15 StartY=-12 StartZ=0 EndX=-7.79258 EndY=-12 EndZ=0
    g15: Circle CenterX=-6.2215 CenterY=-2 CenterZ=0 NormalX=0 NormalY=0 NormalZ=1 AngleXU=0 Radius=1
    g16: Circle CenterX=-6.22762 CenterY=-2.58724 CenterZ=0 NormalX=0 NormalY=0 NormalZ=1 AngleXU=0 Radius=1
    g17: Circle CenterX=-6.32538 CenterY=-4 CenterZ=0 NormalX=0 NormalY=0 NormalZ=1 AngleXU=0 Radius=1
    g18: BSplineCurve PolesCount=3 KnotsCount=2 Degree=2 IsPeriodic=0
    g19: GeomPoint X=-6.2215 Y=-2 Z=0
    g20: GeomPoint X=-6.32538 Y=-4 Z=0
    g21: Circle CenterX=-6.48644 CenterY=-5.99526 CenterZ=0 NormalX=0 NormalY=0 NormalZ=1 AngleXU=0 Radius=1
    g22: Circle CenterX=-6.58486 CenterY=-6.99526 CenterZ=0 NormalX=0 NormalY=0 NormalZ=1 AngleXU=0 Radius=1
    g23: Circle CenterX=-6.77343 CenterY=-8 CenterZ=0 NormalX=0 NormalY=0 NormalZ=1 AngleXU=0 Radius=1
    g24: BSplineCurve PolesCount=3 KnotsCount=2 Degree=2 IsPeriodic=0
    g25: GeomPoint X=-6.48644 Y=-5.99526 Z=0
    g26: GeomPoint X=-6.77343 Y=-8 Z=0
    g27: Circle CenterX=-7.19003 CenterY=-10 CenterZ=0 NormalX=0 NormalY=0 NormalZ=1 AngleXU=0 Radius=1
    g28: Circle CenterX=-7.44407 CenterY=-11.0915 CenterZ=0 NormalX=0 NormalY=0 NormalZ=1 AngleXU=0 Radius=1
    g29: Circle CenterX=-7.79258 CenterY=-12 CenterZ=0 NormalX=0 NormalY=0 NormalZ=1 AngleXU=0 Radius=1
    g30: BSplineCurve PolesCount=3 KnotsCount=2 Degree=2 IsPeriodic=0
    g31: GeomPoint X=-7.19003 Y=-10 Z=0
    g32: GeomPoint X=-7.79258 Y=-12 Z=0
    g33: Circle CenterX=-8.70761 CenterY=-14 CenterZ=0 NormalX=0 NormalY=0 NormalZ=1 AngleXU=0 Radius=1
    g34: Circle CenterX=-9.33087 CenterY=-15.1837 CenterZ=0 NormalX=0 NormalY=0 NormalZ=1 AngleXU=0 Radius=1
    g35: Circle CenterX=-10.1571 CenterY=-16 CenterZ=0 NormalX=0 NormalY=0 NormalZ=1 AngleXU=0 Radius=1
    g36: BSplineCurve PolesCount=3 KnotsCount=2 Degree=2 IsPeriodic=0
    g37: GeomPoint X=-8.70761 Y=-14 Z=0
    g38: GeomPoint X=-10.1571 Y=-16 Z=0
    g39: Circle CenterX=-12.8401 CenterY=-17.6958 CenterZ=0 NormalX=0 NormalY=0 NormalZ=1 AngleXU=0 Radius=1
    g40: Circle CenterX=-13.3521 CenterY=-17.9027 CenterZ=0 NormalX=0 NormalY=0 NormalZ=1 AngleXU=0 Radius=1
    g41: Circle CenterX=-14 CenterY=-18 CenterZ=0 NormalX=0 NormalY=0 NormalZ=1 AngleXU=0 Radius=1
    g42: BSplineCurve PolesCount=3 KnotsCount=2 Degree=2 IsPeriodic=0
    g43: GeomPoint X=-12.8401 Y=-17.6958 Z=0
    g44: GeomPoint X=-14 Y=-18 Z=0
    g45: LineSegment StartX=-6.2 StartY=0 StartZ=0 EndX=-7.2 EndY=0 EndZ=0
    g46: LineSegment StartX=-7.2 StartY=0 StartZ=0 EndX=-7.2 EndY=-2 EndZ=0
    g47: LineSegment StartX=-7.2 StartY=-2 StartZ=0 EndX=-6.2215 EndY=-2 EndZ=0
    g48: LineSegment StartX=-6.32538 StartY=-4 StartZ=0 EndX=-7.65538 EndY=-4 EndZ=0
    g49: LineSegment StartX=-7.65538 StartY=-4 StartZ=0 EndX=-7.65538 EndY=-5.99526 EndZ=0
    g50: LineSegment StartX=-7.65538 StartY=-5.99526 StartZ=0 EndX=-6.48644 EndY=-5.99526 EndZ=0
    g51: LineSegment StartX=-6.77343 StartY=-8 StartZ=0 EndX=-8.43343 EndY=-8 EndZ=0
    g52: LineSegment StartX=-8.43343 StartY=-8 StartZ=0 EndX=-8.43343 EndY=-10 EndZ=0
    g53: LineSegment StartX=-8.43343 StartY=-10 StartZ=0 EndX=-7.19003 EndY=-10 EndZ=0
  constraints (112):
    c: Horizontal(g0)
    c: Distance(g0) = 2
    c: Block(g0)
    c: Vertical(g1)
    c: Coincident(g2,g0)
    c: Vertical(g2)
    c: Block(g2)
    c: Coincident(g6,g2)
    c: Weight(g3) = 1
    c: Equal(g3,g4)
    c: Equal(g3,g5)
    c: InternalAlignment(g3,g6)
    c: InternalAlignment(g4,g6)
    c: InternalAlignment(g5,g6)
    c: InternalAlignment(g7,g6)
    c: InternalAlignment(g8,g6)
    c: Block(g6)
    c: Coincident(g9,g1)
    c: Coincident(g9,g6)
    c: Horizontal(g9)
    c: Vertical(g10)
    c: Block(g10)
    c: Horizontal(g11)
    c: Block(g11)
    c: Coincident(g12,g10)
    c: Horizontal(g12)
    c: Block(g12)
    c: Coincident(g13,g11)
    c: Vertical(g13)
    c: Block(g13)
    c: Coincident(g14,g10)
    c: Horizontal(g14)
    c: Block(g14)
    c: Block(g9)
    c: Block(g1)
    c: Weight(g15) = 1
    c: Equal(g15,g16)
    c: Equal(g15,g17)
    c: InternalAlignment(g15,g18)
    c: InternalAlignment(g16,g18)
    c: InternalAlignment(g17,g18)
    c: InternalAlignment(g19,g18)
    c: InternalAlignment(g20,g18)
    c: Weight(g21) = 1
    c: Equal(g21,g22)
    c: Equal(g21,g23)
    c: InternalAlignment(g21,g24)
    c: InternalAlignment(g22,g24)
    c: InternalAlignment(g23,g24)
    c: InternalAlignment(g25,g24)
    c: InternalAlignment(g26,g24)
    c: Weight(g27) = 1
    c: Equal(g27,g28)
    c: Equal(g27,g29)
    c: Coincident(g30,g14)
    c: InternalAlignment(g27,g30)
    c: InternalAlignment(g28,g30)
    c: InternalAlignment(g29,g30)
    c: InternalAlignment(g31,g30)
    c: InternalAlignment(g32,g30)
    c: Coincident(g36,g12)
    c: Weight(g33) = 1
    c: Equal(g33,g34)
    c: Equal(g33,g35)
    c: Coincident(g36,g11)
    c: InternalAlignment(g33,g36)
    c: InternalAlignment(g34,g36)
    c: InternalAlignment(g35,g36)
    c: InternalAlignment(g37,g36)
    c: InternalAlignment(g38,g36)
    c: Coincident(g42,g13)
    c: Weight(g39) = 1
    c: Equal(g39,g40)
    c: Equal(g39,g41)
    c: Coincident(g42,g1)
    c: InternalAlignment(g39,g42)
    c: InternalAlignment(g40,g42)
    c: InternalAlignment(g41,g42)
    c: InternalAlignment(g43,g42)
    c: InternalAlignment(g44,g42)
    c: Block(g18)
    c: Block(g24)
    c: Block(g30)
    c: Block(g36)
    c: Block(g42)
    c: Horizontal(g45)
    c: Coincident(g45,g0)
    c: Vertical(g46)
    c: Coincident(g46,g45)
    c: Coincident(g47,g46)
    c: Coincident(g47,g18)
    c: Horizontal(g47)
    c: Block(g46)
    c: Coincident(g48,g18)
    c: Horizontal(g48)
    c: Distance(g48) = 1.33
    c: Vertical(g49)
    c: Coincident(g49,g48)
    c: Coincident(g50,g49)
    c: Coincident(g50,g24)
    c: Horizontal(g50)
    c: Tangent(g50,g22)
    c: Horizontal(g51)
    c: Coincident(g51,g24)
    c: Block(g51)
    c: Vertical(g52)
    c: Block(g52)
    c: Coincident(g52,g51)
    c: Coincident(g53,g52)
    c: Coincident(g53,g30)
    c: Horizontal(g53)
    c: Distance(g1) = 8.5
FEATURE [Part::Feature] Face024
  shape: bbox 9.8 x 26.5 x 2e-07 mm, 1 faces, 0 solids (baked)
FEATURE [Part::Revolution] Revolve024
  Angle = 360
  Axis = (0,1,0)
  Base = (0,0,0)
  FaceMakerClass = Part::FaceMakerBullseye
  Placement = pos=(0,0,0) rot=(0,0,1;1.5708rad)
  Solid = false
  Source = -> Face024
  Symmetric = false
FEATURE [Part::Feature] Face025
  shape: bbox 9.8 x 26.5 x 2e-07 mm, 1 faces, 0 solids (baked)
FEATURE [Part::Revolution] Revolve025
  Angle = 360
  Axis = (0,1,0)
  Base = (0,0,0)
  FaceMakerClass = Part::FaceMakerBullseye
  Placement = pos=(0,0,0) rot=(0,0,1;1.5708rad)
  Solid = false
  Source = -> Face025
  Symmetric = false
FEATURE [Part::MultiFuse] Fusion033
  Placement = pos=(-18,19,36) rot=(0,0,1;0rad)
  Shapes = -> [Revolve025,Revolve024]
FEATURE [Part::Cylinder] Cylinder014
  Angle = 360
  AttacherType = Attacher::AttachEngine3D
  Height = 20
  Placement = pos=(0,0,36.15) rot=(0,0,1;0rad)
  Radius = 14.3
FEATURE [Part::Cylinder] Cylinder015
  Angle = 360
  AttacherType = Attacher::AttachEngine3D
  Height = 10
  Placement = pos=(0,0,36.15) rot=(0,0,1;0rad)
  Radius = 4
FEATURE [Part::MultiFuse] Fusion034  label="removeToCreteHoleForPlugHousing004"
  Placement = pos=(-42,19,36) rot=(0,1,0;1.5708rad)
  Shapes = -> [Cylinder014,Cylinder015]
FEATURE [Part::Cut] Cut008  label="top004"
  Base = -> Cut004
  Placement = pos=(-1,0,0) rot=(0,0,1;0rad)
  Tool = -> Fusion034
FEATURE [Part::Box] Box005  label="Cube005"
  AttacherType = Attacher::AttachEngine3D
  Height = 28
  Length = 3
  Placement = pos=(110.7,19,22) rot=(0,0,1;0rad)
  Width = 15.7
FEATURE [Part::Cylinder] Cylinder016
  Angle = 360
  AttacherType = Attacher::AttachEngine3D
  Height = 10
  Placement = pos=(0,0,36.15) rot=(0,0,1;0rad)
  Radius = 4
FEATURE [Part::Cylinder] Cylinder017
  Angle = 360
  AttacherType = Attacher::AttachEngine3D
  Height = 20
  Placement = pos=(0,0,36.15) rot=(0,0,1;0rad)
  Radius = 10.3
FEATURE [Part::MultiFuse] Fusion035  label="removeToCreteHoleForPlugHousing005"
  Placement = pos=(70,19,36) rot=(0,1,0;1.5708rad)
  Shapes = -> [Cylinder017,Cylinder016]
FEATURE [Part::Cut] Cut009  label="plugHousingTab001"
  Base = -> Box005
  Placement = pos=(-107.4,-14,0) rot=(0,0,1;0rad)
  Tool = -> Fusion035
FEATURE [Part::Box] Box006  label="Cube006"
  AttacherType = Attacher::AttachEngine3D
  Height = 28
  Length = 3
  Placement = pos=(110.7,19,22) rot=(0,0,1;0rad)
  Width = 15.7
FEATURE [Part::Cylinder] Cylinder018
  Angle = 360
  AttacherType = Attacher::AttachEngine3D
  Height = 10
  Placement = pos=(0,0,36.15) rot=(0,0,1;0rad)
  Radius = 4
FEATURE [Part::Cylinder] Cylinder019
  Angle = 360
  AttacherType = Attacher::AttachEngine3D
  Height = 20
  Placement = pos=(0,0,36.15) rot=(0,0,1;0rad)
  Radius = 10.3
FEATURE [Part::MultiFuse] Fusion036  label="removeToCreteHoleForPlugHousing006"
  Placement = pos=(70,19,36) rot=(0,1,0;1.5708rad)
  Shapes = -> [Cylinder019,Cylinder018]
FEATURE [Part::Cut] Cut010  label="plugHousingTab002"
  Base = -> Box006
  Placement = pos=(-107.4,-14,0) rot=(0,0,1;0rad)
  Tool = -> Fusion036
FEATURE [Part::MultiFuse] Fusion037
  Placement = pos=(9.6,23,0) rot=(0,0,1;3.14159rad)
  Shapes = -> [Cut009,Cut010]
FEATURE [Part::Box] Box  label="Cube"
  AttacherType = Attacher::AttachEngine3D
  Height = 10
  Length = 3
  Placement = pos=(3.3,4,12) rot=(0,0,1;0rad)
  Width = 10
FEATURE [Part::Fillet] Fillet004
  Base = -> Fusion028
  Edges = 1 edges r=2: [Edge25]
FEATURE [Part::Fillet] Fillet005  label="plugHousing046"
  Base = -> Fillet004
  Edges = 1 edges r=2: [Edge8]
FEATURE [Part::Fillet] Fillet006
  Base = -> Box
  Edges = 1 edges r=2: [Edge11]
FEATURE [Part::Box] Box007  label="Cube007"
  AttacherType = Attacher::AttachEngine3D
  Height = 10
  Length = 3
  Placement = pos=(3.3,4,50) rot=(0,0,1;0rad)
  Width = 10
FEATURE [Part::Fillet] Fillet007
  Base = -> Box007
  Edges = 1 edges r=2: [Edge12]
FEATURE [Part::Box] Box008  label="Cube008"
  AttacherType = Attacher::AttachEngine3D
  Height = 28
  Length = 4
  Placement = pos=(5,0,22) rot=(0,0,1;0rad)
  Width = 10
FEATURE [Part::Fillet] Fillet008
  Base = -> Box008
  Edges = 1 edges r=1: [Edge7]
FEATURE [Part::Fillet] Fillet009
  Base = -> Fillet008
  Edges = 1 edges r=2: [Edge5]
FEATURE [Part::Fillet] Fillet010
  Base = -> Fillet009
  Edges = 1 edges r=2: [Edge2]
FEATURE [Sketcher::SketchObject] Sketch009  label="topSketch003"
  FullyConstrained = true
  sketch-geometry (4):
    g0: LineSegment StartX=16.8446 StartY=31.512 StartZ=0 EndX=16.3251 EndY=34.4666 EndZ=0
    g1: ArcOfCircle CenterX=19 CenterY=19.2524 CenterZ=0 NormalX=0 NormalY=0 NormalZ=1 AngleXU=0 Radius=15.4476 StartAngle=1.74483 EndAngle=2.72717
    g2: ArcOfCircle CenterX=19 CenterY=19.2524 CenterZ=0 NormalX=0 NormalY=0 NormalZ=1 AngleXU=0 Radius=12.4476 StartAngle=1.74483 EndAngle=2.73189
    g3: LineSegment StartX=4.86004 StartY=25.4725 StartZ=0 EndX=7.58253 EndY=24.2107 EndZ=0
  constraints (7):
    c: Block(g0)
    c: Coincident(g1,g0)
    c: Coincident(g2,g0)
    c: Coincident(g3,g1)
    c: Coincident(g3,g2)
    c: Block(g1)
    c: Block(g2)
FEATURE [Part::Extrusion] Extrude008
  Base = -> Sketch009
  Dir = (0,0,1)
  DirMode = 2
  FaceMakerClass = Part::FaceMakerBullseye
  LengthFwd = 10
  LengthRev = 0
  Placement = pos=(0,0,31) rot=(0,0,1;0rad)
  Solid = true
  Symmetric = false
FEATURE [Part::Cylinder] Cylinder020
  Angle = 360
  AttacherType = Attacher::AttachEngine3D
  Height = 20
  Placement = pos=(0,0,36.15) rot=(0,0,1;0rad)
  Radius = 8.2
FEATURE [Part::Cylinder] Cylinder021
  Angle = 360
  AttacherType = Attacher::AttachEngine3D
  Height = 10
  Placement = pos=(0,0,36.15) rot=(0,0,1;0rad)
  Radius = 4
FEATURE [Part::MultiFuse] Fusion038  label="removeToCreteHoleForPlugHousing007"
  Placement = pos=(-42,19,36) rot=(0,1,0;1.5708rad)
  Shapes = -> [Cylinder020,Cylinder021]
FEATURE [Part::Cut] Cut011
  Base = -> Extrude008
  Tool = -> Fusion038
FEATURE [Part::Fillet] Fillet011
  Base = -> Cut011
  Edges = 1 edges r=2: [Edge1]
FEATURE [Part::Fillet] Fillet012
  Base = -> Fillet011
  Edges = 1 edges r=2.5: [Edge1]
FEATURE [Part::Fillet] Fillet013
  Base = -> Fillet012
  Edges = 1 edges r=2.5: [Edge2]
FEATURE [Part::Box] Box010  label="Cube010"
  AttacherType = Attacher::AttachEngine3D
  Height = 16
  Length = 8
  Placement = pos=(12.7,31.52,28) rot=(0,0,1;0rad)
  Width = 4
FEATURE [Sketcher::SketchObject] Sketch010  label="topSketch004"
  FullyConstrained = true
  sketch-geometry (4):
    g0: LineSegment StartX=16.8446 StartY=31.512 StartZ=0 EndX=16.3251 EndY=34.4666 EndZ=0
    g1: ArcOfCircle CenterX=19 CenterY=19.2524 CenterZ=0 NormalX=0 NormalY=0 NormalZ=1 AngleXU=0 Radius=15.4476 StartAngle=1.74483 EndAngle=2.72717
    g2: ArcOfCircle CenterX=19 CenterY=19.2524 CenterZ=0 NormalX=0 NormalY=0 NormalZ=1 AngleXU=0 Radius=12.4476 StartAngle=1.74483 EndAngle=2.73189
    g3: LineSegment StartX=4.86004 StartY=25.4725 StartZ=0 EndX=7.58253 EndY=24.2107 EndZ=0
  constraints (7):
    c: Block(g0)
    c: Coincident(g1,g0)
    c: Coincident(g2,g0)
    c: Coincident(g3,g1)
    c: Coincident(g3,g2)
    c: Block(g1)
    c: Block(g2)
FEATURE [Part::Cylinder] Cylinder022
  Angle = 360
  AttacherType = Attacher::AttachEngine3D
  Height = 10
  Placement = pos=(0,0,36.15) rot=(0,0,1;0rad)
  Radius = 4
FEATURE [Sketcher::SketchObject] Sketch011  label="topSketch005"
  FullyConstrained = true
  sketch-geometry (4):
    g0: LineSegment StartX=16.8446 StartY=31.512 StartZ=0 EndX=16.3251 EndY=34.4666 EndZ=0
    g1: ArcOfCircle CenterX=19 CenterY=19.2524 CenterZ=0 NormalX=0 NormalY=0 NormalZ=1 AngleXU=0 Radius=15.4476 StartAngle=1.74483 EndAngle=2.72717
    g2: ArcOfCircle CenterX=19 CenterY=19.2524 CenterZ=0 NormalX=0 NormalY=0 NormalZ=1 AngleXU=0 Radius=12.4476 StartAngle=1.74483 EndAngle=2.73189
    g3: LineSegment StartX=4.86004 StartY=25.4725 StartZ=0 EndX=7.58253 EndY=24.2107 EndZ=0
  constraints (7):
    c: Block(g0)
    c: Coincident(g1,g0)
    c: Coincident(g2,g0)
    c: Coincident(g3,g1)
    c: Coincident(g3,g2)
    c: Block(g1)
    c: Block(g2)
FEATURE [Part::Extrusion] Extrude010
  Base = -> Sketch011
  Dir = (0,0,1)
  DirMode = 2
  FaceMakerClass = Part::FaceMakerBullseye
  LengthFwd = 10.6
  LengthRev = 0
  Placement = pos=(0,0,31) rot=(0,0,1;0rad)
  Solid = true
  Symmetric = false
FEATURE [Part::Cylinder] Cylinder023
  Angle = 360
  AttacherType = Attacher::AttachEngine3D
  Height = 20
  Placement = pos=(0,0,36.15) rot=(0,0,1;0rad)
  Radius = 8.2
FEATURE [Part::MultiFuse] Fusion039  label="removeToCreteHoleForPlugHousing008"
  Placement = pos=(-42,19,36) rot=(0,1,0;1.5708rad)
  Shapes = -> [Cylinder023,Cylinder022]
FEATURE [Part::Cut] Cut012
  Base = -> Extrude010
  Placement = pos=(0,0,-0.3) rot=(0,0,1;0rad)
  Tool = -> Fusion039
FEATURE [Part::Cut] Cut013
  Base = -> Box010
  Tool = -> Cut012
FEATURE [Part::Fillet] Fillet014
  Base = -> Cut013
  Edges = 1 edges r=0.7: [Edge13]
FEATURE [Part::Fillet] Fillet015
  Base = -> Fillet014
  Edges = 1 edges r=0.7: [Edge13]
FEATURE [Part::Fillet] Fillet016
  Base = -> Fillet015
  Edges = 1 edges r=0.7: [Edge16]
FEATURE [Part::Fillet] Fillet017
  Base = -> Fillet016
  Edges = 1 edges r=0.7: [Edge11]
FEATURE [Part::Fillet] Fillet018
  Base = -> Fillet017
  Edges = 1 edges r=0.7: [Edge10]
FEATURE [Part::Fillet] Fillet019
  Base = -> Fillet018
  Edges = 1 edges r=1.2: [Edge5]
FEATURE [Part::Fillet] Fillet020
  Base = -> Fillet019
  Edges = 1 edges r=1.2: [Edge12]
FEATURE [Part::Fillet] Fillet021
  Base = -> Fillet020
  Edges = 1 edges r=2: [Edge1]
  Placement = pos=(0.3,0,0) rot=(0,0,1;0rad)
FEATURE [Part::MultiFuse] Fusion040  label="top005"
  Shapes = -> [Cut008,Fillet021]
FEATURE [Part::MultiFuse] Fusion041  label="wireHolder"
  Shapes = -> [Fusion033,Fillet013]
FEATURE [Part::MultiFuse] Fusion042
  Shapes = -> [Fillet007,Fusion041]
FEATURE [Part::MultiFuse] Fusion043  label="wireHolder001"
  Shapes = -> [Fusion042,Fillet010]
FEATURE [Part::MultiFuse] Fusion044  label="wireHolder002"
  Shapes = -> [Fillet006,Fusion037,Fusion043]
FEATURE [Part::Feature] Face026
  shape: bbox 11 x 6 x 2e-07 mm, 1 faces, 0 solids (baked)
FEATURE [Part::Revolution] Revolve026
  Angle = 360
  Axis = (0,1,0)
  Base = (0,0,0)
  FaceMakerClass = Part::FaceMakerBullseye
  Placement = pos=(30.3,-1,19.7) rot=(0,0,1;0rad)
  Solid = false
  Source = -> Face026
  Symmetric = false
FEATURE [Sketcher::SketchObject] Sketch013  label="topSketch006"
  FullyConstrained = true
  sketch-geometry (13):
    g0: LineSegment StartX=117 StartY=19 StartZ=0 EndX=117 EndY=38 EndZ=0
    g1: ArcOfCircle CenterX=98 CenterY=19 CenterZ=0 NormalX=0 NormalY=0 NormalZ=1 AngleXU=0 Radius=19 StartAngle=5.7297 EndAngle=6.28319
    g2: LineSegment StartX=0 StartY=3 StartZ=0 EndX=0 EndY=19 EndZ=0
    g3: LineSegment StartX=19 StartY=38 StartZ=0 EndX=117 EndY=38 EndZ=0
    g4: ArcOfCircle CenterX=19 CenterY=19 CenterZ=0 NormalX=0 NormalY=0 NormalZ=1 AngleXU=0 Radius=19 StartAngle=1.5708 EndAngle=3.14159
    g5: ArcOfCircle CenterX=19 CenterY=19 CenterZ=0 NormalX=0 NormalY=0 NormalZ=1 AngleXU=0 Radius=16 StartAngle=1.5708 EndAngle=3.14159
    g6: ArcOfCircle CenterX=98 CenterY=19 CenterZ=0 NormalX=0 NormalY=0 NormalZ=1 AngleXU=0 Radius=16 StartAngle=5.60905 EndAngle=6.28319
    g7: LineSegment StartX=114 StartY=19 StartZ=0 EndX=114 EndY=35 EndZ=0
    g8: LineSegment StartX=110.5 StartY=9.01251 StartZ=0 EndX=114.163 EndY=9.01251 EndZ=0
    g9: LineSegment StartX=114 StartY=35 StartZ=0 EndX=19 EndY=35 EndZ=0
    g10: LineSegment StartX=0 StartY=3 StartZ=0 EndX=0 EndY=0 EndZ=0
    g11: LineSegment StartX=3 StartY=0 StartZ=0 EndX=0 EndY=0 EndZ=0
    g12: LineSegment StartX=3 StartY=19 StartZ=0 EndX=3 EndY=0 EndZ=0
  constraints (33):
    c: Vertical(g0)
    c: Distance(g0) = 19
    c: Block(g0)
    c: Coincident(g1,g0)
    c: Block(g1)
    c: Vertical(g2)
    c: Block(g2)
    c: Coincident(g3,g0)
    c: Horizontal(g3)
    c: Distance(g3) = 98
    c: Coincident(g4,g3)
    c: Coincident(g4,g2)
    c: Block(g4)
    c: Coincident(g5,g4)
    c: Coincident(g6,g1)
    c: Block(g6)
    c: Block(g5)
    c: Coincident(g7,g6)
    c: Vertical(g7)
    c: Coincident(g8,g6)
    c: Coincident(g8,g1)
    c: Coincident(g9,g7)
    c: Coincident(g9,g5)
    c: Horizontal(g9)
    c: Tangent(g9,g5)
    c: Coincident(g10,g2)
    c: Distance(g10) = 3
    c: Vertical(g10)
    c: Coincident(g11,g10)
    c: Horizontal(g11)
    c: Coincident(g12,g5)
    c: Coincident(g12,g11)
    c: Vertical(g12)
FEATURE [Part::Extrusion] Extrude011  label="top006"
  Base = -> Sketch013
  Dir = (0,0,1)
  DirMode = 2
  FaceMakerClass = Part::FaceMakerBullseye
  LengthFwd = 72
  LengthRev = 0
  Solid = true
  Symmetric = false
FEATURE [Sketcher::SketchObject] Sketch014
  FullyConstrained = true
  MapMode = 3
  Placement = pos=(0,0,0) rot=(1,0,0;1.5708rad)
  Support = -> [Extrude011]
  sketch-geometry (8):
    g0: Circle CenterX=80.351 CenterY=-67.6202 CenterZ=0 NormalX=0 NormalY=0 NormalZ=1 AngleXU=0 Radius=2
    g1: Circle CenterX=80.351 CenterY=-67.6202 CenterZ=0 NormalX=0 NormalY=0 NormalZ=1 AngleXU=0 Radius=3
    g2: Circle CenterX=80.351 CenterY=-4.92017 CenterZ=0 NormalX=0 NormalY=0 NormalZ=1 AngleXU=0 Radius=2
    g3: Circle CenterX=80.351 CenterY=-4.92017 CenterZ=0 NormalX=0 NormalY=0 NormalZ=1 AngleXU=0 Radius=3
    g4: Circle CenterX=23.851 CenterY=-4.92017 CenterZ=0 NormalX=0 NormalY=0 NormalZ=1 AngleXU=0 Radius=2
    g5: Circle CenterX=23.851 CenterY=-4.92017 CenterZ=0 NormalX=0 NormalY=0 NormalZ=1 AngleXU=0 Radius=3
    g6: Circle CenterX=23.851 CenterY=-67.6202 CenterZ=0 NormalX=0 NormalY=0 NormalZ=1 AngleXU=0 Radius=2
    g7: Circle CenterX=23.851 CenterY=-67.6202 CenterZ=0 NormalX=0 NormalY=0 NormalZ=1 AngleXU=0 Radius=3
  constraints (8):
    c: Block(g3)
    c: Block(g2)
    c: Block(g1)
    c: Block(g0)
    c: Block(g6)
    c: Block(g7)
    c: Block(g4)
    c: Block(g5)
FEATURE [Part::Feature] Face027
  shape: bbox 11 x 6 x 2e-07 mm, 1 faces, 0 solids (baked)
FEATURE [Part::Revolution] Revolve027
  Angle = 360
  Axis = (0,1,0)
  Base = (0,0,0)
  FaceMakerClass = Part::FaceMakerBullseye
  Placement = pos=(30.3,-1,51.7) rot=(0,0,1;0rad)
  Solid = false
  Source = -> Face027
  Symmetric = false
FEATURE [Part::Feature] Face028
  shape: bbox 11 x 6 x 2e-07 mm, 1 faces, 0 solids (baked)
FEATURE [Part::Revolution] Revolve028
  Angle = 360
  Axis = (0,1,0)
  Base = (0,0,0)
  FaceMakerClass = Part::FaceMakerBullseye
  Placement = pos=(62.3,-1,19.7) rot=(0,0,1;0rad)
  Solid = false
  Source = -> Face028
  Symmetric = false
FEATURE [Part::Feature] Face029
  shape: bbox 11 x 6 x 2e-07 mm, 1 faces, 0 solids (baked)
FEATURE [Part::Revolution] Revolve029
  Angle = 360
  Axis = (0,1,0)
  Base = (0,0,0)
  FaceMakerClass = Part::FaceMakerBullseye
  Placement = pos=(62.3,-1,51.7) rot=(0,0,1;0rad)
  Solid = false
  Source = -> Face029
  Symmetric = false
FEATURE [Part::Feature] Wire
  shape: bbox 11 x 5.2 x 2e-07 mm, 0 faces, 0 solids (baked)
FEATURE [Part::Revolution] Revolve030
  Angle = 360
  Axis = (0,1,0)
  Base = (0,0,0)
  FaceMakerClass = Part::FaceMakerBullseye
  Placement = pos=(30.3,38,19.7) rot=(0,0,1;0rad)
  Solid = true
  Source = -> Wire
  Symmetric = false
FEATURE [Part::Feature] Wire001
  shape: bbox 11 x 5.2 x 2e-07 mm, 0 faces, 0 solids (baked)
FEATURE [Part::Revolution] Revolve031
  Angle = 360
  Axis = (0,1,0)
  Base = (0,0,0)
  FaceMakerClass = Part::FaceMakerBullseye
  Placement = pos=(30.3,38,51.7) rot=(0,0,1;0rad)
  Solid = true
  Source = -> Wire001
  Symmetric = false
FEATURE [Part::Feature] Wire002
  shape: bbox 11 x 5.2 x 2e-07 mm, 0 faces, 0 solids (baked)
FEATURE [Part::Revolution] Revolve032
  Angle = 360
  Axis = (0,1,0)
  Base = (0,0,0)
  FaceMakerClass = Part::FaceMakerBullseye
  Placement = pos=(62.3,38,51.7) rot=(0,0,1;0rad)
  Solid = true
  Source = -> Wire002
  Symmetric = false
FEATURE [Part::Feature] Wire003
  shape: bbox 11 x 5.2 x 2e-07 mm, 0 faces, 0 solids (baked)
FEATURE [Part::Revolution] Revolve033
  Angle = 360
  Axis = (0,1,0)
  Base = (0,0,0)
  FaceMakerClass = Part::FaceMakerBullseye
  Placement = pos=(62.3,38,19.7) rot=(0,0,1;0rad)
  Solid = true
  Source = -> Wire003
  Symmetric = false
FEATURE [Part::MultiFuse] Fusion045  label="altRandScrewHousing"
  Shapes = -> [Revolve029,Revolve027,Revolve028,Revolve026]
FEATURE [Part::MultiFuse] Fusion046  label="fanScrewHousing"
  Shapes = -> [Revolve033,Revolve032,Revolve031,Revolve030]
FEATURE [Sketcher::SketchObject] Sketch015
  FullyConstrained = true
  sketch-geometry (17):
    g0: Circle CenterX=-3.5 CenterY=23.5 CenterZ=0 NormalX=0 NormalY=0 NormalZ=1 AngleXU=0 Radius=1
    g1: Circle CenterX=-1 CenterY=15.25 CenterZ=0 NormalX=0 NormalY=0 NormalZ=1 AngleXU=0 Radius=1
    g2: Circle CenterX=-3.5 CenterY=7 CenterZ=0 NormalX=0 NormalY=0 NormalZ=1 AngleXU=0 Radius=1
    g3: BSplineCurve PolesCount=3 KnotsCount=2 Degree=2 IsPeriodic=0
    g4: GeomPoint X=-3.5 Y=23.5 Z=0
    g5: GeomPoint X=-3.5 Y=7 Z=0
    g6: Circle CenterX=-4.8 CenterY=30.5 CenterZ=0 NormalX=0 NormalY=0 NormalZ=1 AngleXU=0 Radius=1
    g7: Circle CenterX=-3.5 CenterY=30.5 CenterZ=0 NormalX=0 NormalY=0 NormalZ=1 AngleXU=0 Radius=1
    g8: Circle CenterX=-3.5 CenterY=29.2 CenterZ=0 NormalX=0 NormalY=0 NormalZ=1 AngleXU=0 Radius=1
    g9: BSplineCurve PolesCount=3 KnotsCount=2 Degree=2 IsPeriodic=0
    g10: GeomPoint X=-4.8 Y=30.5 Z=0
    g11: GeomPoint X=-3.5 Y=29.2 Z=0
    g12: LineSegment StartX=-3.5 StartY=29.2 StartZ=0 EndX=-3.5 EndY=23.5 EndZ=0
    g13: LineSegment StartX=-4.8 StartY=30.5 StartZ=0 EndX=0 EndY=30.5 EndZ=0
    g14: LineSegment StartX=-3.5 StartY=0.3 StartZ=0 EndX=0 EndY=0.3 EndZ=0
    g15: LineSegment StartX=-3.5 StartY=0.3 StartZ=0 EndX=-3.5 EndY=7 EndZ=0
    g16: LineSegment StartX=0 StartY=0.3 StartZ=0 EndX=0 EndY=30.5 EndZ=0
  constraints (33):
    c: Weight(g0) = 1
    c: Equal(g0,g1)
    c: Equal(g0,g2)
    c: InternalAlignment(g0,g3)
    c: InternalAlignment(g1,g3)
    c: InternalAlignment(g2,g3)
    c: InternalAlignment(g4,g3)
    c: InternalAlignment(g5,g3)
    c: Block(g3)
    c: Weight(g6) = 1
    c: Equal(g6,g7)
    c: Equal(g6,g8)
    c: InternalAlignment(g6,g9)
    c: InternalAlignment(g7,g9)
    c: InternalAlignment(g8,g9)
    c: InternalAlignment(g10,g9)
    c: InternalAlignment(g11,g9)
    c: Block(g9)
    c: Coincident(g12,g9)
    c: Coincident(g12,g3)
    c: Vertical(g12)
    c: Coincident(g13,g9)
    c: Horizontal(g13)
    c: Distance(g13) = 4.8
    c: Horizontal(g14)
    c: Block(g14)
    c: Coincident(g15,g14)
    c: Coincident(g15,g3)
    c: Vertical(g15)
    c: Coincident(g16,g14)
    c: Coincident(g16,g13)
    c: Vertical(g16)
    c: Tangent(g16,g1)
FEATURE [Sketcher::SketchObject] Sketch016
  FullyConstrained = true
  sketch-geometry (16):
    g0: Circle CenterX=-3.5 CenterY=23.5 CenterZ=0 NormalX=0 NormalY=0 NormalZ=1 AngleXU=0 Radius=1
    g1: Circle CenterX=-1 CenterY=15.25 CenterZ=0 NormalX=0 NormalY=0 NormalZ=1 AngleXU=0 Radius=1
    g2: Circle CenterX=-3.5 CenterY=7 CenterZ=0 NormalX=0 NormalY=0 NormalZ=1 AngleXU=0 Radius=1
    g3: BSplineCurve PolesCount=3 KnotsCount=2 Degree=2 IsPeriodic=0
    g4: GeomPoint X=-3.5 Y=23.5 Z=0
    g5: GeomPoint X=-3.5 Y=7 Z=0
    g6: LineSegment StartX=-3.5 StartY=28.2 StartZ=0 EndX=-3.5 EndY=23.5 EndZ=0
    g7: LineSegment StartX=0 StartY=29.5 StartZ=0 EndX=0 EndY=30 EndZ=0
    g8: LineSegment StartX=-3.5 StartY=28.2 StartZ=0 EndX=-3.5 EndY=30 EndZ=0
    g9: LineSegment StartX=0 StartY=30 StartZ=0 EndX=0 EndY=30.5 EndZ=0
    g10: LineSegment StartX=0 StartY=30.5 StartZ=0 EndX=-3.5 EndY=30.5 EndZ=0
    g11: LineSegment StartX=-3.5 StartY=30.5 StartZ=0 EndX=-3.5 EndY=30 EndZ=0
    g12: LineSegment StartX=0 StartY=29.5 StartZ=0 EndX=0 EndY=5 EndZ=0
    g13: LineSegment StartX=-3.5 StartY=0.3 StartZ=0 EndX=-3.5 EndY=7 EndZ=0
    g14: LineSegment StartX=-3.5 StartY=0.3 StartZ=0 EndX=0 EndY=0.3 EndZ=0
    g15: LineSegment StartX=0 StartY=5 StartZ=0 EndX=0 EndY=0.3 EndZ=0
  constraints (39):
    c: Weight(g0) = 1
    c: Equal(g0,g1)
    c: Equal(g0,g2)
    c: InternalAlignment(g0,g3)
    c: InternalAlignment(g1,g3)
    c: InternalAlignment(g2,g3)
    c: InternalAlignment(g4,g3)
    c: InternalAlignment(g5,g3)
    c: Block(g3)
    c: Coincident(g6,g3)
    c: Vertical(g6)
    c: Vertical(g7)
    c: Distance(g7) = 0.5
    c: Coincident(g8,g6)
    c: Vertical(g8)
    c: Block(g6)
    c: Block(g7)
    c: Vertical(g9)
    c: Equal(g7,g9) = 0.5
    c: Block(g9)
    c: Coincident(g9,g7)
    c: Horizontal(g10)
    c: Coincident(g10,g9)
    c: Coincident(g11,g10)
    c: Coincident(g11,g8)
    c: Vertical(g11)
    c: Block(g11)
    c: Coincident(g12,g7)
    c: Vertical(g12)
    c: Coincident(g13,g3)
    c: Vertical(g13)
    c: Distance(g13) = 6.7
    c: Coincident(g14,g13)
    c: Horizontal(g14)
    c: Block(g14)
    c: Coincident(g15,g12)
    c: Coincident(g15,g14)
    c: Vertical(g15)
    c: Block(g15)
FEATURE [Sketcher::SketchObject] Sketch017
  FullyConstrained = true
  sketch-geometry (11):
    g0: LineSegment StartX=-3.5 StartY=1e-16 StartZ=0 EndX=-1.6 EndY=1e-16 EndZ=0
    g1: LineSegment StartX=-1.6 StartY=1e-16 StartZ=0 EndX=-1.6 EndY=1.5 EndZ=0
    g2: LineSegment StartX=-3.5 StartY=1.5 StartZ=0 EndX=-1.6 EndY=1.5 EndZ=0
    g3: LineSegment StartX=-3.5 StartY=1e-16 StartZ=0 EndX=-4.8 EndY=1e-16 EndZ=0
    g4: Circle CenterX=-3.5 CenterY=1.3 CenterZ=0 NormalX=0 NormalY=0 NormalZ=1 AngleXU=0 Radius=1
    g5: Circle CenterX=-3.5 CenterY=1e-16 CenterZ=0 NormalX=0 NormalY=0 NormalZ=1 AngleXU=0 Radius=1
    g6: Circle CenterX=-4.8 CenterY=1e-16 CenterZ=0 NormalX=0 NormalY=0 NormalZ=1 AngleXU=0 Radius=1
    g7: BSplineCurve PolesCount=3 KnotsCount=2 Degree=2 IsPeriodic=0
    g8: GeomPoint X=-3.5 Y=1.3 Z=0
    g9: GeomPoint X=-4.8 Y=1e-16 Z=0
    g10: LineSegment StartX=-3.5 StartY=1.3 StartZ=0 EndX=-3.5 EndY=1.5 EndZ=0
  constraints (24):
    c: Horizontal(g0)
    c: Distance(g0) = 1.9
    c: Block(g0)
    c: Coincident(g1,g0)
    c: Vertical(g1)
    c: Coincident(g2,g1)
    c: Horizontal(g2)
    c: Coincident(g3,g0)
    c: Horizontal(g3)
    c: Distance(g3) = 1.3
    c: Weight(g4) = 1
    c: Equal(g4,g5)
    c: Coincident(g5,g0)
    c: Equal(g4,g6)
    c: Coincident(g7,g3)
    c: InternalAlignment(g4,g7)
    c: InternalAlignment(g5,g7)
    c: InternalAlignment(g6,g7)
    c: InternalAlignment(g8,g7)
    c: InternalAlignment(g9,g7)
    c: Coincident(g10,g7)
    c: Coincident(g10,g2)
    c: Vertical(g10)
    c: Block(g10)
FEATURE [Part::Feature] Face035
  shape: bbox 3.2 x 1.5 x 2e-07 mm, 1 faces, 0 solids (baked)
FEATURE [Part::Revolution] Revolve039  label="backCaseScrewRetainer"
  Angle = 360
  Axis = (0,1,0)
  Base = (0,0,0)
  FaceMakerClass = Part::FaceMakerBullseye
  Placement = pos=(12.5,3,62) rot=(0,0,1;0rad)
  Solid = false
  Source = -> Face035
  Symmetric = false
FEATURE [Part::Feature] Face036
  shape: bbox 3.2 x 1.5 x 2e-07 mm, 1 faces, 0 solids (baked)
FEATURE [Part::Feature] Face039
  shape: bbox 4.8 x 30.2 x 2e-07 mm, 1 faces, 0 solids (baked)
FEATURE [Part::Revolution] Revolve043  label="frontCaseScrewPost002"
  Angle = 360
  Axis = (0,1,0)
  Base = (0,0,0)
  FaceMakerClass = Part::FaceMakerBullseye
  Placement = pos=(89.5,4.5,3.5) rot=(0,0,1;0rad)
  Solid = false
  Source = -> Face039
  Symmetric = false
FEATURE [Part::Feature] Face042
  shape: bbox 4.8 x 30.2 x 2e-07 mm, 1 faces, 0 solids (baked)
FEATURE [Part::Revolution] Revolve046  label="frontCaseScrewPost003"
  Angle = 360
  Axis = (0,1,0)
  Base = (0,0,0)
  FaceMakerClass = Part::FaceMakerBullseye
  Placement = pos=(89.5,4.5,68.5) rot=(0,0,1;0rad)
  Solid = false
  Source = -> Face042
  Symmetric = false
FEATURE [Part::Feature] Face043
  shape: bbox 3.2 x 1.5 x 2e-07 mm, 1 faces, 0 solids (baked)
FEATURE [Part::Revolution] Revolve047  label="frontCaseScrewRetainer002"
  Angle = 360
  Axis = (0,1,0)
  Base = (0,0,0)
  FaceMakerClass = Part::FaceMakerBullseye
  Placement = pos=(89.5,3,68.5) rot=(0,0,1;0rad)
  Solid = false
  Source = -> Face043
  Symmetric = false
FEATURE [Part::Feature] Face044
  shape: bbox 3.2 x 1.5 x 2e-07 mm, 1 faces, 0 solids (baked)
FEATURE [Part::Revolution] Revolve048  label="frontCaseScrewRetainer003"
  Angle = 360
  Axis = (0,1,0)
  Base = (0,0,0)
  FaceMakerClass = Part::FaceMakerBullseye
  Placement = pos=(89.5,3,3.5) rot=(0,0,1;0rad)
  Solid = false
  Source = -> Face044
  Symmetric = false
FEATURE [App::MeasureDistance] Distance002  label="Distance: 1.67 mm"
  Distance = 1.66921
  P1 = (99.2361,4.7524,71.7)
  P2 = (99.2347,6.42161,71.7)
FEATURE [Sketcher::SketchObject] Sketch018
  FullyConstrained = true
  sketch-geometry (7):
    g0: LineSegment StartX=0 StartY=0 StartZ=0 EndX=0 EndY=6 EndZ=0
    g1: Circle CenterX=0 CenterY=0 CenterZ=0 NormalX=0 NormalY=0 NormalZ=1 AngleXU=0 Radius=1
    g2: Circle CenterX=8 CenterY=6 CenterZ=0 NormalX=0 NormalY=0 NormalZ=1 AngleXU=0 Radius=1
    g3: BSplineCurve PolesCount=3 KnotsCount=2 Degree=2 IsPeriodic=0
    g4: GeomPoint X=0 Y=0 Z=0
    g5: GeomPoint X=8 Y=6 Z=0
    g6: LineSegment StartX=0 StartY=6 StartZ=0 EndX=8 EndY=6 EndZ=0
  constraints (14):
    c: Coincident(g0,g-1)
    c: Distance(g0) = 6
    c: Vertical(g0)
    c: Coincident(g3,g0)
    c: Weight(g1) = 1
    c: Equal(g1,g2)
    c: InternalAlignment(g1,g3)
    c: InternalAlignment(g2,g3)
    c: InternalAlignment(g4,g3)
    c: InternalAlignment(g5,g3)
    c: Block(g3)
    c: Coincident(g6,g0)
    c: Coincident(g6,g3)
    c: Horizontal(g6)
FEATURE [Part::Extrusion] Extrude012  label="caseScrewPillarBracket"
  Base = -> Sketch018
  Dir = (0,0,1)
  DirMode = 2
  FaceMakerClass = Part::FaceMakerBullseye
  LengthFwd = 2.4
  LengthRev = 0
  Placement = pos=(15.76,29,8.8) rot=(0,1,0;0rad)
  Solid = true
  Symmetric = false
FEATURE [Sketcher::SketchObject] Sketch019
  FullyConstrained = true
  sketch-geometry (7):
    g0: LineSegment StartX=0 StartY=0 StartZ=0 EndX=0 EndY=6 EndZ=0
    g1: Circle CenterX=0 CenterY=0 CenterZ=0 NormalX=0 NormalY=0 NormalZ=1 AngleXU=0 Radius=1
    g2: Circle CenterX=8 CenterY=6 CenterZ=0 NormalX=0 NormalY=0 NormalZ=1 AngleXU=0 Radius=1
    g3: BSplineCurve PolesCount=3 KnotsCount=2 Degree=2 IsPeriodic=0
    g4: GeomPoint X=0 Y=0 Z=0
    g5: GeomPoint X=8 Y=6 Z=0
    g6: LineSegment StartX=0 StartY=6 StartZ=0 EndX=8 EndY=6 EndZ=0
  constraints (14):
    c: Coincident(g0,g-1)
    c: Distance(g0) = 6
    c: Vertical(g0)
    c: Coincident(g3,g0)
    c: Weight(g1) = 1
    c: Equal(g1,g2)
    c: InternalAlignment(g1,g3)
    c: InternalAlignment(g2,g3)
    c: InternalAlignment(g4,g3)
    c: InternalAlignment(g5,g3)
    c: Block(g3)
    c: Coincident(g6,g0)
    c: Coincident(g6,g3)
    c: Horizontal(g6)
FEATURE [Part::Extrusion] Extrude013  label="caseScrewPillarBracket001"
  Base = -> Sketch019
  Dir = (0,0,1)
  DirMode = 2
  FaceMakerClass = Part::FaceMakerBullseye
  LengthFwd = 2.4
  LengthRev = 0
  Placement = pos=(15.76,29,60.8) rot=(0,0,1;0rad)
  Solid = true
  Symmetric = false
FEATURE [Sketcher::SketchObject] Sketch020
  FullyConstrained = true
  sketch-geometry (7):
    g0: LineSegment StartX=0 StartY=0 StartZ=0 EndX=0 EndY=6 EndZ=0
    g1: Circle CenterX=0 CenterY=0 CenterZ=0 NormalX=0 NormalY=0 NormalZ=1 AngleXU=0 Radius=1
    g2: Circle CenterX=8 CenterY=6 CenterZ=0 NormalX=0 NormalY=0 NormalZ=1 AngleXU=0 Radius=1
    g3: BSplineCurve PolesCount=3 KnotsCount=2 Degree=2 IsPeriodic=0
    g4: GeomPoint X=0 Y=0 Z=0
    g5: GeomPoint X=8 Y=6 Z=0
    g6: LineSegment StartX=0 StartY=6 StartZ=0 EndX=8 EndY=6 EndZ=0
  constraints (14):
    c: Coincident(g0,g-1)
    c: Distance(g0) = 6
    c: Vertical(g0)
    c: Coincident(g3,g0)
    c: Weight(g1) = 1
    c: Equal(g1,g2)
    c: InternalAlignment(g1,g3)
    c: InternalAlignment(g2,g3)
    c: InternalAlignment(g4,g3)
    c: InternalAlignment(g5,g3)
    c: Block(g3)
    c: Coincident(g6,g0)
    c: Coincident(g6,g3)
    c: Horizontal(g6)
FEATURE [Part::Extrusion] Extrude014  label="caseScrewPillarBracket002"
  Base = -> Sketch020
  Dir = (0,0,1)
  DirMode = 2
  FaceMakerClass = Part::FaceMakerBullseye
  LengthFwd = 2.4
  LengthRev = 0
  Placement = pos=(13.7,29,13.26) rot=(0,-1,0;1.5708rad)
  Solid = true
  Symmetric = false
FEATURE [Sketcher::SketchObject] Sketch021
  FullyConstrained = true
  sketch-geometry (7):
    g0: LineSegment StartX=0 StartY=0 StartZ=0 EndX=0 EndY=6 EndZ=0
    g1: Circle CenterX=0 CenterY=0 CenterZ=0 NormalX=0 NormalY=0 NormalZ=1 AngleXU=0 Radius=1
    g2: Circle CenterX=8 CenterY=6 CenterZ=0 NormalX=0 NormalY=0 NormalZ=1 AngleXU=0 Radius=1
    g3: BSplineCurve PolesCount=3 KnotsCount=2 Degree=2 IsPeriodic=0
    g4: GeomPoint X=0 Y=0 Z=0
    g5: GeomPoint X=8 Y=6 Z=0
    g6: LineSegment StartX=0 StartY=6 StartZ=0 EndX=8 EndY=6 EndZ=0
  constraints (14):
    c: Coincident(g0,g-1)
    c: Distance(g0) = 6
    c: Vertical(g0)
    c: Coincident(g3,g0)
    c: Weight(g1) = 1
    c: Equal(g1,g2)
    c: InternalAlignment(g1,g3)
    c: InternalAlignment(g2,g3)
    c: InternalAlignment(g4,g3)
    c: InternalAlignment(g5,g3)
    c: Block(g3)
    c: Coincident(g6,g0)
    c: Coincident(g6,g3)
    c: Horizontal(g6)
FEATURE [Part::Extrusion] Extrude015  label="caseScrewPillarBracket003"
  Base = -> Sketch021
  Dir = (0,0,1)
  DirMode = 2
  FaceMakerClass = Part::FaceMakerBullseye
  LengthFwd = 2.4
  LengthRev = 0
  Placement = pos=(11.3,29,58.74) rot=(0,1,0;1.5708rad)
  Solid = true
  Symmetric = false
FEATURE [Sketcher::SketchObject] Sketch022
  FullyConstrained = true
  sketch-geometry (7):
    g0: LineSegment StartX=0 StartY=0 StartZ=0 EndX=0 EndY=6 EndZ=0
    g1: Circle CenterX=0 CenterY=0 CenterZ=0 NormalX=0 NormalY=0 NormalZ=1 AngleXU=0 Radius=1
    g2: Circle CenterX=8 CenterY=6 CenterZ=0 NormalX=0 NormalY=0 NormalZ=1 AngleXU=0 Radius=1
    g3: BSplineCurve PolesCount=3 KnotsCount=2 Degree=2 IsPeriodic=0
    g4: GeomPoint X=0 Y=0 Z=0
    g5: GeomPoint X=8 Y=6 Z=0
    g6: LineSegment StartX=0 StartY=6 StartZ=0 EndX=8 EndY=6 EndZ=0
  constraints (14):
    c: Coincident(g0,g-1)
    c: Distance(g0) = 6
    c: Vertical(g0)
    c: Coincident(g3,g0)
    c: Weight(g1) = 1
    c: Equal(g1,g2)
    c: InternalAlignment(g1,g3)
    c: InternalAlignment(g2,g3)
    c: InternalAlignment(g4,g3)
    c: InternalAlignment(g5,g3)
    c: Block(g3)
    c: Coincident(g6,g0)
    c: Coincident(g6,g3)
    c: Horizontal(g6)
FEATURE [Part::Extrusion] Extrude016  label="caseScrewPillarBracket004"
  Base = -> Sketch022
  Dir = (0,0,1)
  DirMode = 2
  FaceMakerClass = Part::FaceMakerBullseye
  LengthFwd = 2.4
  LengthRev = 0
  Placement = pos=(88.3,29,65.23) rot=(0,1,0;1.5708rad)
  Solid = true
  Symmetric = false
FEATURE [Sketcher::SketchObject] Sketch023
  FullyConstrained = true
  sketch-geometry (7):
    g0: LineSegment StartX=0 StartY=0 StartZ=0 EndX=0 EndY=6 EndZ=0
    g1: Circle CenterX=0 CenterY=0 CenterZ=0 NormalX=0 NormalY=0 NormalZ=1 AngleXU=0 Radius=1
    g2: Circle CenterX=8 CenterY=6 CenterZ=0 NormalX=0 NormalY=0 NormalZ=1 AngleXU=0 Radius=1
    g3: BSplineCurve PolesCount=3 KnotsCount=2 Degree=2 IsPeriodic=0
    g4: GeomPoint X=0 Y=0 Z=0
    g5: GeomPoint X=8 Y=6 Z=0
    g6: LineSegment StartX=0 StartY=6 StartZ=0 EndX=8 EndY=6 EndZ=0
  constraints (14):
    c: Coincident(g0,g-1)
    c: Distance(g0) = 6
    c: Vertical(g0)
    c: Coincident(g3,g0)
    c: Weight(g1) = 1
    c: Equal(g1,g2)
    c: InternalAlignment(g1,g3)
    c: InternalAlignment(g2,g3)
    c: InternalAlignment(g4,g3)
    c: InternalAlignment(g5,g3)
    c: Block(g3)
    c: Coincident(g6,g0)
    c: Coincident(g6,g3)
    c: Horizontal(g6)
FEATURE [Part::Extrusion] Extrude017  label="caseScrewPillarBracket005"
  Base = -> Sketch023
  Dir = (0,0,1)
  DirMode = 2
  FaceMakerClass = Part::FaceMakerBullseye
  LengthFwd = 2.4
  LengthRev = 0
  Placement = pos=(90.7,29,6.77) rot=(0,-1,0;1.5708rad)
  Solid = true
  Symmetric = false
FEATURE [Sketcher::SketchObject] Sketch024
  FullyConstrained = true
  sketch-geometry (7):
    g0: LineSegment StartX=0 StartY=0 StartZ=0 EndX=0 EndY=6 EndZ=0
    g1: Circle CenterX=0 CenterY=0 CenterZ=0 NormalX=0 NormalY=0 NormalZ=1 AngleXU=0 Radius=1
    g2: Circle CenterX=8 CenterY=6 CenterZ=0 NormalX=0 NormalY=0 NormalZ=1 AngleXU=0 Radius=1
    g3: BSplineCurve PolesCount=3 KnotsCount=2 Degree=2 IsPeriodic=0
    g4: GeomPoint X=0 Y=0 Z=0
    g5: GeomPoint X=8 Y=6 Z=0
    g6: LineSegment StartX=0 StartY=6 StartZ=0 EndX=8 EndY=6 EndZ=0
  constraints (14):
    c: Coincident(g0,g-1)
    c: Distance(g0) = 6
    c: Vertical(g0)
    c: Coincident(g3,g0)
    c: Weight(g1) = 1
    c: Equal(g1,g2)
    c: InternalAlignment(g1,g3)
    c: InternalAlignment(g2,g3)
    c: InternalAlignment(g4,g3)
    c: InternalAlignment(g5,g3)
    c: Block(g3)
    c: Coincident(g6,g0)
    c: Coincident(g6,g3)
    c: Horizontal(g6)
FEATURE [Part::Extrusion] Extrude018  label="caseScrewPillarBracket006"
  Base = -> Sketch024
  Dir = (0,0,1)
  DirMode = 2
  FaceMakerClass = Part::FaceMakerBullseye
  LengthFwd = 2.4
  LengthRev = 0
  Placement = pos=(103.7,29,6.77) rot=(0,-1,0;1.5708rad)
  Solid = true
  Symmetric = false
FEATURE [Sketcher::SketchObject] Sketch025
  FullyConstrained = true
  sketch-geometry (7):
    g0: LineSegment StartX=0 StartY=0 StartZ=0 EndX=0 EndY=6 EndZ=0
    g1: Circle CenterX=0 CenterY=0 CenterZ=0 NormalX=0 NormalY=0 NormalZ=1 AngleXU=0 Radius=1
    g2: Circle CenterX=8 CenterY=6 CenterZ=0 NormalX=0 NormalY=0 NormalZ=1 AngleXU=0 Radius=1
    g3: BSplineCurve PolesCount=3 KnotsCount=2 Degree=2 IsPeriodic=0
    g4: GeomPoint X=0 Y=0 Z=0
    g5: GeomPoint X=8 Y=6 Z=0
    g6: LineSegment StartX=0 StartY=6 StartZ=0 EndX=8 EndY=6 EndZ=0
  constraints (14):
    c: Coincident(g0,g-1)
    c: Distance(g0) = 6
    c: Vertical(g0)
    c: Coincident(g3,g0)
    c: Weight(g1) = 1
    c: Equal(g1,g2)
    c: InternalAlignment(g1,g3)
    c: InternalAlignment(g2,g3)
    c: InternalAlignment(g4,g3)
    c: InternalAlignment(g5,g3)
    c: Block(g3)
    c: Coincident(g6,g0)
    c: Coincident(g6,g3)
    c: Horizontal(g6)
FEATURE [Part::Extrusion] Extrude019  label="caseScrewPillarBracket007"
  Base = -> Sketch025
  Dir = (0,0,1)
  DirMode = 2
  FaceMakerClass = Part::FaceMakerBullseye
  LengthFwd = 2.4
  LengthRev = 0
  Placement = pos=(101.3,29,65.23) rot=(0,1,0;1.5708rad)
  Solid = true
  Symmetric = false
FEATURE [Part::Box] Box011  label="frontCaseScrewPillarBracket"
  AttacherType = Attacher::AttachEngine3D
  Height = 2.4
  Length = 16
  Placement = pos=(87,28,2.3) rot=(0,0,1;0rad)
  Width = 7
FEATURE [Part::Box] Box012  label="frontCaseScrewPillarBracket001"
  AttacherType = Attacher::AttachEngine3D
  Height = 2.4
  Length = 16
  Placement = pos=(87,28,67.3) rot=(0,0,1;0rad)
  Width = 7
FEATURE [Sketcher::SketchObject] Sketch026
  FullyConstrained = true
  sketch-geometry (17):
    g0: Circle CenterX=-3.5 CenterY=23.5 CenterZ=0 NormalX=0 NormalY=0 NormalZ=1 AngleXU=0 Radius=1
    g1: Circle CenterX=-1 CenterY=15.25 CenterZ=0 NormalX=0 NormalY=0 NormalZ=1 AngleXU=0 Radius=1
    g2: Circle CenterX=-3.5 CenterY=7 CenterZ=0 NormalX=0 NormalY=0 NormalZ=1 AngleXU=0 Radius=1
    g3: BSplineCurve PolesCount=3 KnotsCount=2 Degree=2 IsPeriodic=0
    g4: GeomPoint X=-3.5 Y=23.5 Z=0
    g5: GeomPoint X=-3.5 Y=7 Z=0
    g6: Circle CenterX=-4.8 CenterY=30.5 CenterZ=0 NormalX=0 NormalY=0 NormalZ=1 AngleXU=0 Radius=1
    g7: Circle CenterX=-3.5 CenterY=30.5 CenterZ=0 NormalX=0 NormalY=0 NormalZ=1 AngleXU=0 Radius=1
    g8: Circle CenterX=-3.5 CenterY=29.2 CenterZ=0 NormalX=0 NormalY=0 NormalZ=1 AngleXU=0 Radius=1
    g9: BSplineCurve PolesCount=3 KnotsCount=2 Degree=2 IsPeriodic=0
    g10: GeomPoint X=-4.8 Y=30.5 Z=0
    g11: GeomPoint X=-3.5 Y=29.2 Z=0
    g12: LineSegment StartX=-3.5 StartY=29.2 StartZ=0 EndX=-3.5 EndY=23.5 EndZ=0
    g13: LineSegment StartX=-4.8 StartY=30.5 StartZ=0 EndX=0 EndY=30.5 EndZ=0
    g14: LineSegment StartX=-3.5 StartY=5 StartZ=0 EndX=-3.5 EndY=7 EndZ=0
    g15: LineSegment StartX=0 StartY=5 StartZ=0 EndX=0 EndY=30.5 EndZ=0
    g16: LineSegment StartX=-3.5 StartY=5 StartZ=0 EndX=0 EndY=5 EndZ=0
  constraints (33):
    c: Weight(g0) = 1
    c: Equal(g0,g1)
    c: Equal(g0,g2)
    c: InternalAlignment(g0,g3)
    c: InternalAlignment(g1,g3)
    c: InternalAlignment(g2,g3)
    c: InternalAlignment(g4,g3)
    c: InternalAlignment(g5,g3)
    c: Block(g3)
    c: Weight(g6) = 1
    c: Equal(g6,g7)
    c: Equal(g6,g8)
    c: InternalAlignment(g6,g9)
    c: InternalAlignment(g7,g9)
    c: InternalAlignment(g8,g9)
    c: InternalAlignment(g10,g9)
    c: InternalAlignment(g11,g9)
    c: Block(g9)
    c: Coincident(g12,g9)
    c: Coincident(g12,g3)
    c: Vertical(g12)
    c: Coincident(g13,g9)
    c: Horizontal(g13)
    c: Distance(g13) = 4.8
    c: Coincident(g14,g3)
    c: Vertical(g14)
    c: Coincident(g15,g13)
    c: Vertical(g15)
    c: Tangent(g15,g1)
    c: Distance(g14) = 2
    c: Coincident(g16,g14)
    c: Horizontal(g16)
    c: Coincident(g15,g16)
FEATURE [Part::Feature] Face050
  shape: bbox 4.8 x 25.5 x 2e-07 mm, 1 faces, 0 solids (baked)
FEATURE [Part::Revolution] Revolve054  label="moreFrontCaseScrewPost001"
  Angle = 360
  Axis = (0,1,0)
  Base = (0,0,0)
  FaceMakerClass = Part::FaceMakerBullseye
  Placement = pos=(102.5,4.5,3.5) rot=(0,0,1;0rad)
  Solid = false
  Source = -> Face050
  Symmetric = false
FEATURE [Part::Feature] Face051
  shape: bbox 4.8 x 25.5 x 2e-07 mm, 1 faces, 0 solids (baked)
FEATURE [Part::Revolution] Revolve055  label="moreFrontCaseScrewPost002"
  Angle = 360
  Axis = (0,1,0)
  Base = (0,0,0)
  FaceMakerClass = Part::FaceMakerBullseye
  Placement = pos=(102.5,4.5,68.5) rot=(0,0,1;0rad)
  Solid = false
  Source = -> Face051
  Symmetric = false
FEATURE [Sketcher::SketchObject] Sketch027
  FullyConstrained = true
  sketch-geometry (10):
    g0: LineSegment StartX=-1.6 StartY=4.7 StartZ=0 EndX=-1.6 EndY=1.7 EndZ=0
    g1: LineSegment StartX=-3.5 StartY=4.7 StartZ=0 EndX=-1.6 EndY=4.7 EndZ=0
    g2: LineSegment StartX=-1.6 StartY=1.7 StartZ=0 EndX=-1.6 EndY=1.5 EndZ=0
    g3: LineSegment StartX=-1.6 StartY=1.5 StartZ=0 EndX=-5.2 EndY=1.5 EndZ=0
    g4: Circle CenterX=-3.5 CenterY=4.7 CenterZ=0 NormalX=0 NormalY=0 NormalZ=1 AngleXU=0 Radius=1
    g5: Circle CenterX=-3.59627 CenterY=2.99743 CenterZ=0 NormalX=0 NormalY=0 NormalZ=1 AngleXU=0 Radius=1
    g6: Circle CenterX=-5.2 CenterY=1.5 CenterZ=0 NormalX=0 NormalY=0 NormalZ=1 AngleXU=0 Radius=1
    g7: BSplineCurve PolesCount=3 KnotsCount=2 Degree=2 IsPeriodic=0
    g8: GeomPoint X=-3.5 Y=4.7 Z=0
    g9: GeomPoint X=-5.2 Y=1.5 Z=0
  constraints (23):
    c: Vertical(g0)
    c: Distance(g0) = 3
    c: Coincident(g1,g0)
    c: Horizontal(g1)
    c: Block(g0)
    c: Block(g1)
    c: Coincident(g2,g0)
    c: Vertical(g2)
    c: Distance(g2) = 0.2
    c: Coincident(g3,g2)
    c: Horizontal(g3)
    c: Block(g3)
    c: Coincident(g7,g1)
    c: Weight(g4) = 1
    c: Equal(g4,g5)
    c: Equal(g4,g6)
    c: Coincident(g7,g3)
    c: InternalAlignment(g4,g7)
    c: InternalAlignment(g5,g7)
    c: InternalAlignment(g6,g7)
    c: InternalAlignment(g8,g7)
    c: InternalAlignment(g9,g7)
    c: Block(g7)
FEATURE [Sketcher::SketchObject] Sketch028
  FullyConstrained = true
  sketch-geometry (18):
    g0: LineSegment StartX=0 StartY=3e-16 StartZ=0 EndX=0 EndY=1.7 EndZ=0
    g1: LineSegment StartX=-3.5 StartY=0 StartZ=0 EndX=-3.5 EndY=0.9 EndZ=0
    g2: Circle CenterX=-2.7 CenterY=1.7 CenterZ=0 NormalX=0 NormalY=0 NormalZ=1 AngleXU=0 Radius=1
    g3: Circle CenterX=-3.5 CenterY=1.7 CenterZ=0 NormalX=0 NormalY=0 NormalZ=1 AngleXU=0 Radius=1
    g4: Circle CenterX=-3.5 CenterY=0.9 CenterZ=0 NormalX=0 NormalY=0 NormalZ=1 AngleXU=0 Radius=1
    g5: BSplineCurve PolesCount=3 KnotsCount=2 Degree=2 IsPeriodic=0
    g6: GeomPoint X=-2.7 Y=1.7 Z=0
    g7: GeomPoint X=-3.5 Y=0.9 Z=0
    g8: LineSegment StartX=-3.5 StartY=0 StartZ=0 EndX=-3.5 EndY=-7 EndZ=0
    g9: LineSegment StartX=0 StartY=3e-16 StartZ=0 EndX=0 EndY=-7 EndZ=0
    g10: LineSegment StartX=-3.5 StartY=-7 StartZ=0 EndX=0 EndY=-7 EndZ=0
    g11: LineSegment StartX=-2.7 StartY=1.7 StartZ=0 EndX=-1.6 EndY=1.7 EndZ=0
    g12: LineSegment StartX=0 StartY=1.7 StartZ=0 EndX=0 EndY=4.5 EndZ=0
    g13: LineSegment StartX=0 StartY=4.5 StartZ=0 EndX=0 EndY=10.8 EndZ=0
    g14: LineSegment StartX=0 StartY=10.8 StartZ=0 EndX=-2 EndY=10.8 EndZ=0
    g15: LineSegment StartX=-1.6 StartY=4.7 StartZ=0 EndX=-1.6 EndY=1.7 EndZ=0
    g16: LineSegment StartX=-1.6 StartY=4.7 StartZ=0 EndX=-2 EndY=4.7 EndZ=0
    g17: LineSegment StartX=-2 StartY=4.7 StartZ=0 EndX=-2 EndY=10.8 EndZ=0
  constraints (44):
    c: Vertical(g0)
    c: Vertical(g1)
    c: Distance(g1) = 0.9
    c: Block(g0)
    c: Distance(g0) = 1.7
    c: Weight(g2) = 1
    c: Equal(g2,g3)
    c: Equal(g2,g4)
    c: Coincident(g5,g1)
    c: InternalAlignment(g2,g5)
    c: InternalAlignment(g3,g5)
    c: InternalAlignment(g4,g5)
    c: InternalAlignment(g6,g5)
    c: InternalAlignment(g7,g5)
    c: Block(g5)
    c: Coincident(g8,g1)
    c: Vertical(g8)
    c: Distance(g8) = 7
    c: Vertical(g9)
    c: Equal(g8,g9) = 7
    c: Coincident(g9,g0)
    c: Coincident(g10,g8)
    c: Coincident(g10,g9)
    c: Horizontal(g10)
    c: Coincident(g11,g5)
    c: Horizontal(g11)
    c: Coincident(g12,g0)
    c: Vertical(g12)
    c: Distance(g12) = 2.8
    c: Coincident(g13,g12)
    c: Vertical(g13)
    c: Distance(g13) = 6.3
    c: Coincident(g14,g13)
    c: Horizontal(g14)
    c: Distance(g14) = 2
    c: Vertical(g15)
    c: Distance(g15) = 3
    c: Block(g11)
    c: Coincident(g15,g11)
    c: Coincident(g16,g15)
    c: Horizontal(g16)
    c: Coincident(g17,g16)
    c: Coincident(g17,g14)
    c: Vertical(g17)
FEATURE [Part::Revolution] Revolve040  label="backCaseScrewRetainer001"
  Angle = 360
  Axis = (0,1,0)
  Base = (0,0,0)
  FaceMakerClass = Part::FaceMakerBullseye
  Placement = pos=(12.5,3,10) rot=(0,0,1;0rad)
  Solid = false
  Source = -> Face036
  Symmetric = false
FEATURE [Part::Feature] Face055
  shape: bbox 3.5 x 30.2 x 2e-07 mm, 1 faces, 0 solids (baked)
FEATURE [Part::Revolution] Revolve059  label="backCaseScrewPost"
  Angle = 360
  Axis = (0,1,0)
  Base = (0,0,0)
  FaceMakerClass = Part::FaceMakerBullseye
  Placement = pos=(12.5,4.5,10) rot=(0,0,1;0rad)
  Solid = false
  Source = -> Face055
  Symmetric = false
FEATURE [Part::Feature] Face056
  shape: bbox 3.5 x 30.2 x 2e-07 mm, 1 faces, 0 solids (baked)
FEATURE [Part::Revolution] Revolve060  label="backCaseScrewPost001"
  Angle = 360
  Axis = (0,1,0)
  Base = (0,0,0)
  FaceMakerClass = Part::FaceMakerBullseye
  Placement = pos=(12.5,4.5,62) rot=(0,0,1;0rad)
  Solid = false
  Source = -> Face056
  Symmetric = false
FEATURE [Part::Feature] Face057
  shape: bbox 3.5 x 17.8 x 2e-07 mm, 1 faces, 0 solids (baked)
FEATURE [Part::Revolution] Revolve061  label="removeToCreateScrewAndThreadedInsertHole"
  Angle = 360
  Axis = (0,1,0)
  Base = (0,0,0)
  FaceMakerClass = Part::FaceMakerBullseye
  Placement = pos=(12.5,0,10) rot=(0,0,1;0rad)
  Solid = false
  Source = -> Face057
  Symmetric = false
FEATURE [Part::Feature] Face058
  shape: bbox 3.5 x 17.8 x 2e-07 mm, 1 faces, 0 solids (baked)
FEATURE [Part::Revolution] Revolve062  label="removeToCreateScrewAndThreadedInsertHole001"
  Angle = 360
  Axis = (0,1,0)
  Base = (0,0,0)
  FaceMakerClass = Part::FaceMakerBullseye
  Placement = pos=(12.5,0,62) rot=(0,0,1;0rad)
  Solid = false
  Source = -> Face058
  Symmetric = false
FEATURE [Part::Feature] Face059
  shape: bbox 3.5 x 17.8 x 2e-07 mm, 1 faces, 0 solids (baked)
FEATURE [Part::Revolution] Revolve063  label="removeToCreateScrewAndThreadedInsertHole002"
  Angle = 360
  Axis = (0,1,0)
  Base = (0,0,0)
  FaceMakerClass = Part::FaceMakerBullseye
  Placement = pos=(89.5,0,68.5) rot=(0,0,1;0rad)
  Solid = false
  Source = -> Face059
  Symmetric = false
FEATURE [Part::Feature] Face060
  shape: bbox 3.5 x 17.8 x 2e-07 mm, 1 faces, 0 solids (baked)
FEATURE [Part::Revolution] Revolve064  label="removeToCreateScrewAndThreadedInsertHole003"
  Angle = 360
  Axis = (0,1,0)
  Base = (0,0,0)
  FaceMakerClass = Part::FaceMakerBullseye
  Placement = pos=(89.5,0,3.5) rot=(0,0,1;0rad)
  Solid = false
  Source = -> Face060
  Symmetric = false
FEATURE [Part::Feature] Face061
  shape: bbox 3.5 x 17.8 x 2e-07 mm, 1 faces, 0 solids (baked)
FEATURE [Part::Revolution] Revolve065  label="removeToCreateScrewAndThreadedInsertHole004"
  Angle = 360
  Axis = (0,1,0)
  Base = (0,0,0)
  FaceMakerClass = Part::FaceMakerBullseye
  Placement = pos=(102.5,4.7,3.5) rot=(0,0,1;0rad)
  Solid = false
  Source = -> Face061
  Symmetric = false
FEATURE [Part::Feature] Face062
  shape: bbox 3.5 x 17.8 x 2e-07 mm, 1 faces, 0 solids (baked)
FEATURE [Part::Revolution] Revolve066  label="removeToCreateScrewAndThreadedInsertHole005"
  Angle = 360
  Axis = (0,1,0)
  Base = (0,0,0)
  FaceMakerClass = Part::FaceMakerBullseye
  Placement = pos=(102.5,4.7,68.5) rot=(0,0,1;0rad)
  Solid = false
  Source = -> Face062
  Symmetric = false
FEATURE [Part::MultiFuse] Fusion047  label="makeHoles"
  Shapes = -> [Revolve066,Revolve065,Revolve064,Revolve063,Revolve062,Revolve061]
FEATURE [Part::Feature] Face063
  shape: bbox 3.6 x 3.2 x 2e-07 mm, 1 faces, 0 solids (baked)
FEATURE [Part::Revolution] Revolve067  label="moreFrontCaseScrewRetainer002"
  Angle = 360
  Axis = (0,1,0)
  Base = (0,0,0)
  FaceMakerClass = Part::FaceMakerBullseye
  Placement = pos=(102.5,4.5,68.5) rot=(0,0,1;0rad)
  Solid = false
  Source = -> Face063
  Symmetric = false
FEATURE [Part::Feature] Face064
  shape: bbox 3.6 x 3.2 x 2e-07 mm, 1 faces, 0 solids (baked)
FEATURE [Part::Revolution] Revolve068  label="moreFrontCaseScrewRetainer003"
  Angle = 360
  Axis = (0,1,0)
  Base = (0,0,0)
  FaceMakerClass = Part::FaceMakerBullseye
  Placement = pos=(102.5,4.5,3.5) rot=(0,0,1;0rad)
  Solid = false
  Source = -> Face064
  Symmetric = false
FEATURE [Part::Feature] Face065
  shape: bbox 3.5 x 17.8 x 2e-07 mm, 1 faces, 0 solids (baked)
FEATURE [Part::Revolution] Revolve069  label="removeToCreateScrewAndThreadedInsertHole006"
  Angle = 360
  Axis = (0,1,0)
  Base = (0,0,0)
  FaceMakerClass = Part::FaceMakerBullseye
  Placement = pos=(12.5,0,10) rot=(0,0,1;0rad)
  Solid = false
  Source = -> Face065
  Symmetric = false
FEATURE [Part::Feature] Face066
  shape: bbox 3.5 x 17.8 x 2e-07 mm, 1 faces, 0 solids (baked)
FEATURE [Part::Revolution] Revolve070  label="removeToCreateScrewAndThreadedInsertHole007"
  Angle = 360
  Axis = (0,1,0)
  Base = (0,0,0)
  FaceMakerClass = Part::FaceMakerBullseye
  Placement = pos=(12.5,0,62) rot=(0,0,1;0rad)
  Solid = false
  Source = -> Face066
  Symmetric = false
FEATURE [Part::Feature] Face067
  shape: bbox 3.5 x 17.8 x 2e-07 mm, 1 faces, 0 solids (baked)
FEATURE [Part::Revolution] Revolve071  label="removeToCreateScrewAndThreadedInsertHole008"
  Angle = 360
  Axis = (0,1,0)
  Base = (0,0,0)
  FaceMakerClass = Part::FaceMakerBullseye
  Placement = pos=(89.5,0,68.5) rot=(0,0,1;0rad)
  Solid = false
  Source = -> Face067
  Symmetric = false
FEATURE [Part::Feature] Face068
  shape: bbox 3.5 x 17.8 x 2e-07 mm, 1 faces, 0 solids (baked)
FEATURE [Part::Revolution] Revolve072  label="removeToCreateScrewAndThreadedInsertHole009"
  Angle = 360
  Axis = (0,1,0)
  Base = (0,0,0)
  FaceMakerClass = Part::FaceMakerBullseye
  Placement = pos=(89.5,0,3.5) rot=(0,0,1;0rad)
  Solid = false
  Source = -> Face068
  Symmetric = false
FEATURE [Part::Feature] Face069
  shape: bbox 3.5 x 17.8 x 2e-07 mm, 1 faces, 0 solids (baked)
FEATURE [Part::Feature] Face070
  shape: bbox 3.5 x 17.8 x 2e-07 mm, 1 faces, 0 solids (baked)
FEATURE [Part::Revolution] Revolve073  label="removeToCreateScrewAndThreadedInsertHole010"
  Angle = 360
  Axis = (0,1,0)
  Base = (0,0,0)
  FaceMakerClass = Part::FaceMakerBullseye
  Placement = pos=(102.5,4.7,3.5) rot=(0,0,1;0rad)
  Solid = false
  Source = -> Face069
  Symmetric = false
FEATURE [Part::Revolution] Revolve074  label="removeToCreateScrewAndThreadedInsertHole011"
  Angle = 360
  Axis = (0,1,0)
  Base = (0,0,0)
  FaceMakerClass = Part::FaceMakerBullseye
  Placement = pos=(102.5,4.7,68.5) rot=(0,0,1;0rad)
  Solid = false
  Source = -> Face070
  Symmetric = false
FEATURE [Part::MultiFuse] Fusion048  label="makeHoles001"
  Shapes = -> [Revolve074,Revolve073,Revolve072,Revolve071,Revolve070,Revolve069]
FEATURE [Part::MultiFuse] Fusion049  label="caseScrewRetainers"
  Shapes = -> [Revolve067,Revolve068,Revolve048,Revolve047,Revolve039,Revolve040]
FEATURE [Part::Cut] Cut015  label="caseScrewRetainers001"
  Base = -> Fusion049
  Tool = -> Fusion048
FEATURE [Part::MultiFuse] Fusion050  label="casePillars"
  Shapes = -> [Revolve055,Revolve054,Revolve043,Revolve046,Revolve059,Revolve060]
FEATURE [Part::Feature] Face071 .. Face076  x6 (patterned run collapsed; names and placements below)
  shape: bbox 3.5 x 17.8 x 2e-07 mm, 1 faces, 0 solids (baked)
FEATURE [Part::Revolution] Revolve075  label="removeToCreateScrewAndThreadedInsertHole012"
  Angle = 360
  Axis = (0,1,0)
  Base = (0,0,0)
  FaceMakerClass = Part::FaceMakerBullseye
  Placement = pos=(12.5,0,10) rot=(0,0,1;0rad)
  Solid = false
  Source = -> Face071
  Symmetric = false
FEATURE [Part::Revolution] Revolve076  label="removeToCreateScrewAndThreadedInsertHole013"
  Angle = 360
  Axis = (0,1,0)
  Base = (0,0,0)
  FaceMakerClass = Part::FaceMakerBullseye
  Placement = pos=(12.5,0,62) rot=(0,0,1;0rad)
  Solid = false
  Source = -> Face072
  Symmetric = false
FEATURE [Part::Revolution] Revolve077  label="removeToCreateScrewAndThreadedInsertHole014"
  Angle = 360
  Axis = (0,1,0)
  Base = (0,0,0)
  FaceMakerClass = Part::FaceMakerBullseye
  Placement = pos=(89.5,0,68.5) rot=(0,0,1;0rad)
  Solid = false
  Source = -> Face073
  Symmetric = false
FEATURE [Part::Revolution] Revolve078  label="removeToCreateScrewAndThreadedInsertHole015"
  Angle = 360
  Axis = (0,1,0)
  Base = (0,0,0)
  FaceMakerClass = Part::FaceMakerBullseye
  Placement = pos=(89.5,0,3.5) rot=(0,0,1;0rad)
  Solid = false
  Source = -> Face074
  Symmetric = false
FEATURE [Part::Revolution] Revolve079  label="removeToCreateScrewAndThreadedInsertHole016"
  Angle = 360
  Axis = (0,1,0)
  Base = (0,0,0)
  FaceMakerClass = Part::FaceMakerBullseye
  Placement = pos=(102.5,4.7,3.5) rot=(0,0,1;0rad)
  Solid = false
  Source = -> Face075
  Symmetric = false
FEATURE [Part::Revolution] Revolve080  label="removeToCreateScrewAndThreadedInsertHole017"
  Angle = 360
  Axis = (0,1,0)
  Base = (0,0,0)
  FaceMakerClass = Part::FaceMakerBullseye
  Placement = pos=(102.5,4.7,68.5) rot=(0,0,1;0rad)
  Solid = false
  Source = -> Face076
  Symmetric = false
FEATURE [Part::MultiFuse] Fusion051  label="makeHoles002"
  Shapes = -> [Revolve080,Revolve079,Revolve078,Revolve077,Revolve076,Revolve075]
FEATURE [Part::Cut] Cut016  label="caesPillars"
  Base = -> Fusion050
  Tool = -> Fusion051
FEATURE [Part::Revolution] Revolve009  label="plugHousing016"
  Angle = 360
  Axis = (0,1,0)
  Base = (0,0,0)
  FaceMakerClass = Part::FaceMakerBullseye
  Placement = pos=(0,0,36.15) rot=(0,0,1;0rad)
  Solid = false
  Source = -> Face012
  Symmetric = false
FEATURE [Part::MultiFuse] Fusion014  label="plugHousing023"
  Placement = pos=(0,0,0) rot=(0,0,1;1.5708rad)
  Shapes = -> [Revolve011,Revolve009]
FEATURE [Part::Revolution] Revolve010  label="plugHousing017"
  Angle = 360
  Axis = (0,1,0)
  Base = (0,0,0)
  FaceMakerClass = Part::FaceMakerBullseye
  Placement = pos=(0,0,36.15) rot=(0,0,1;0rad)
  Solid = false
  Source = -> Face014
  Symmetric = false
FEATURE [Part::MultiFuse] Fusion015  label="plugHousing024"
  Placement = pos=(0,0,0) rot=(0,0,1;1.5708rad)
  Shapes = -> [Revolve010,Revolve015]
FEATURE [Part::Revolution] Revolve014  label="plugHousing026"
  Angle = 360
  Axis = (0,1,0)
  Base = (0,0,0)
  FaceMakerClass = Part::FaceMakerBullseye
  Placement = pos=(0,0,36.15) rot=(0,0,1;0rad)
  Solid = false
  Source = -> Face011
  Symmetric = false
FEATURE [Part::Revolution] Revolve013  label="plugHousing025"
  Angle = 360
  Axis = (0,1,0)
  Base = (0,0,0)
  FaceMakerClass = Part::FaceMakerBullseye
  Placement = pos=(0,0,36.15) rot=(0,0,1;0rad)
  Solid = false
  Source = -> Face015
  Symmetric = false
FEATURE [Part::MultiFuse] Fusion016  label="plugHousing028"
  Placement = pos=(0,19,0) rot=(0,0,1;3.14159rad)
  Shapes = -> [Fusion014,Fusion013]
FEATURE [Part::MultiFuse] Fusion011  label="plugHousing018"
  Placement = pos=(0,0,0) rot=(0,0,1;1.5708rad)
  Shapes = -> [Revolve014,Revolve013]
FEATURE [Part::MultiFuse] Fusion012  label="plugHousing019"
  Placement = pos=(0,19,0) rot=(0,0,1;3.14159rad)
  Shapes = -> [Fusion011,Fusion015]
FEATURE [Part::MultiFuse] Fusion017  label="plugHousing029"
  Placement = pos=(122.621,0,-0.15) rot=(0,0,1;0rad)
  Shapes = -> [Fusion016,Fusion012]
FEATURE [Part::MultiFuse] Fusion052  label="casePillarRetainers"
  Shapes = -> [Extrude012,Extrude013,Extrude014,Extrude015,Extrude016,Extrude017,Extrude018,Extrude019,Box011,Box012]
FEATURE [Part::Feature] Face077
  shape: bbox 3.5 x 17.8 x 2e-07 mm, 1 faces, 0 solids (baked)
FEATURE [Part::Revolution] Revolve081  label="removeToCreateScrewAndThreadedInsertHole018"
  Angle = 360
  Axis = (0,1,0)
  Base = (0,0,0)
  FaceMakerClass = Part::FaceMakerBullseye
  Placement = pos=(62.3,30.3,19.7) rot=(0,0,1;0rad)
  Solid = false
  Source = -> Face077
  Symmetric = false
FEATURE [Part::Feature] Face078
  shape: bbox 3.5 x 17.8 x 2e-07 mm, 1 faces, 0 solids (baked)
FEATURE [Part::Revolution] Revolve082  label="removeToCreateScrewAndThreadedInsertHole019"
  Angle = 360
  Axis = (0,1,0)
  Base = (0,0,0)
  FaceMakerClass = Part::FaceMakerBullseye
  Placement = pos=(62.3,30.3,51.7) rot=(0,0,1;0rad)
  Solid = false
  Source = -> Face078
  Symmetric = false
FEATURE [Part::Feature] Face079
  shape: bbox 3.5 x 17.8 x 2e-07 mm, 1 faces, 0 solids (baked)
FEATURE [Part::Revolution] Revolve083  label="removeToCreateScrewAndThreadedInsertHole020"
  Angle = 360
  Axis = (0,1,0)
  Base = (0,0,0)
  FaceMakerClass = Part::FaceMakerBullseye
  Placement = pos=(30.3,30.3,19.7) rot=(0,0,1;0rad)
  Solid = false
  Source = -> Face079
  Symmetric = false
FEATURE [Part::Feature] Face080
  shape: bbox 3.5 x 17.8 x 2e-07 mm, 1 faces, 0 solids (baked)
FEATURE [Part::Revolution] Revolve084  label="removeToCreateScrewAndThreadedInsertHole021"
  Angle = 360
  Axis = (0,1,0)
  Base = (0,0,0)
  FaceMakerClass = Part::FaceMakerBullseye
  Placement = pos=(30.3,30.3,51.7) rot=(0,0,1;0rad)
  Solid = false
  Source = -> Face080
  Symmetric = false
FEATURE [Part::MultiFuse] Fusion053  label="createThreadedInsertHolesForFan"
  Shapes = -> [Revolve081,Revolve082,Revolve083,Revolve084]
FEATURE [Part::Cut] Cut017  label="fanScrewHousing001"
  Base = -> Fusion046
  Tool = -> Fusion053
FEATURE [Part::Feature] Face081
  shape: bbox 3.5 x 17.8 x 2e-07 mm, 1 faces, 0 solids (baked)
FEATURE [Part::Revolution] Revolve085  label="removeToCreateScrewAndThreadedInsertHole022"
  Angle = 360
  Axis = (0,1,0)
  Base = (0,0,0)
  FaceMakerClass = Part::FaceMakerBullseye
  Placement = pos=(62.3,30.3,19.7) rot=(0,0,1;0rad)
  Solid = false
  Source = -> Face081
  Symmetric = false
FEATURE [Part::Feature] Face082
  shape: bbox 3.5 x 17.8 x 2e-07 mm, 1 faces, 0 solids (baked)
FEATURE [Part::Revolution] Revolve086  label="removeToCreateScrewAndThreadedInsertHole023"
  Angle = 360
  Axis = (0,1,0)
  Base = (0,0,0)
  FaceMakerClass = Part::FaceMakerBullseye
  Placement = pos=(62.3,30.3,51.7) rot=(0,0,1;0rad)
  Solid = false
  Source = -> Face082
  Symmetric = false
FEATURE [Part::Feature] Face083
  shape: bbox 3.5 x 17.8 x 2e-07 mm, 1 faces, 0 solids (baked)
FEATURE [Part::Revolution] Revolve087  label="removeToCreateScrewAndThreadedInsertHole024"
  Angle = 360
  Axis = (0,1,0)
  Base = (0,0,0)
  FaceMakerClass = Part::FaceMakerBullseye
  Placement = pos=(30.3,30.3,19.7) rot=(0,0,1;0rad)
  Solid = false
  Source = -> Face083
  Symmetric = false
FEATURE [Part::Feature] Face084
  shape: bbox 3.5 x 17.8 x 2e-07 mm, 1 faces, 0 solids (baked)
FEATURE [Part::Revolution] Revolve088  label="removeToCreateScrewAndThreadedInsertHole025"
  Angle = 360
  Axis = (0,1,0)
  Base = (0,0,0)
  FaceMakerClass = Part::FaceMakerBullseye
  Placement = pos=(30.3,30.3,51.7) rot=(0,0,1;0rad)
  Solid = false
  Source = -> Face084
  Symmetric = false
FEATURE [Part::MultiFuse] Fusion054  label="createThreadedInsertHolesForFan001"
  Shapes = -> [Revolve085,Revolve086,Revolve087,Revolve088]
FEATURE [Part::Cut] Cut018  label="top007"
  Base = -> Fusion040
  Tool = -> Fusion054
FEATURE [Sketcher::SketchObject] Sketch029
  FullyConstrained = false
  Placement = pos=(0,0,0) rot=(1,0,0;1.5708rad)
  sketch-geometry (24):
    g0: ArcOfCircle CenterX=-4 CenterY=-10.5 CenterZ=0 NormalX=0 NormalY=0 NormalZ=1 AngleXU=0 Radius=1.5 StartAngle=6e-16 EndAngle=3.14159
    g1: ArcOfCircle CenterX=-34.2 CenterY=-10.5 CenterZ=0 NormalX=0 NormalY=0 NormalZ=1 AngleXU=0 Radius=1.5 StartAngle=0 EndAngle=3.14159
    g2: ArcOfCircle CenterX=-34.2 CenterY=-27.7 CenterZ=0 NormalX=0 NormalY=0 NormalZ=1 AngleXU=0 Radius=1.5 StartAngle=3.14159 EndAngle=6.28319
    g3: ArcOfCircle CenterX=-4 CenterY=-27.7 CenterZ=0 NormalX=0 NormalY=0 NormalZ=1 AngleXU=0 Radius=1.5 StartAngle=3.1416 EndAngle=6.28319
    g4: ArcOfCircle CenterX=-10 CenterY=-4.3 CenterZ=0 NormalX=0 NormalY=0 NormalZ=1 AngleXU=0 Radius=1.5 StartAngle=2e-16 EndAngle=3.14159
    g5: ArcOfCircle CenterX=-16.1 CenterY=-1.8 CenterZ=0 NormalX=0 NormalY=0 NormalZ=1 AngleXU=0 Radius=1.5 StartAngle=5e-16 EndAngle=3.14159
    g6: ArcOfCircle CenterX=-22.1 CenterY=-1.8 CenterZ=0 NormalX=0 NormalY=0 NormalZ=1 AngleXU=0 Radius=1.5 StartAngle=5e-16 EndAngle=3.14159
    g7: ArcOfCircle CenterX=-28.2 CenterY=-4.3 CenterZ=0 NormalX=0 NormalY=0 NormalZ=1 AngleXU=0 Radius=1.5 StartAngle=2e-16 EndAngle=3.14159
    g8: ArcOfCircle CenterX=-10 CenterY=-33.9 CenterZ=0 NormalX=0 NormalY=0 NormalZ=1 AngleXU=0 Radius=1.5 StartAngle=3.14159 EndAngle=6.28319
    g9: ArcOfCircle CenterX=-16.1 CenterY=-36.4 CenterZ=0 NormalX=0 NormalY=0 NormalZ=1 AngleXU=0 Radius=1.5 StartAngle=3.14159 EndAngle=6.28319
    g10: ArcOfCircle CenterX=-22.1 CenterY=-36.4 CenterZ=0 NormalX=0 NormalY=0 NormalZ=1 AngleXU=0 Radius=1.5 StartAngle=3.14159 EndAngle=6.28319
    g11: ArcOfCircle CenterX=-28.2 CenterY=-33.9 CenterZ=0 NormalX=0 NormalY=0 NormalZ=1 AngleXU=0 Radius=1.5 StartAngle=3.14159 EndAngle=6.28319
    g12: LineSegment StartX=-35.7 StartY=-10.5 StartZ=0 EndX=-35.7 EndY=-27.7 EndZ=0
    g13: LineSegment StartX=-32.7 StartY=-10.5 StartZ=0 EndX=-32.7 EndY=-27.7 EndZ=0
    g14: LineSegment StartX=-29.7 StartY=-33.9 StartZ=0 EndX=-29.7 EndY=-4.3 EndZ=0
    g15: LineSegment StartX=-26.7 StartY=-33.9 StartZ=0 EndX=-26.7 EndY=-4.3 EndZ=0
    g16: LineSegment StartX=-2.5 StartY=-10.5 StartZ=0 EndX=-2.5 EndY=-27.7 EndZ=0
    g17: LineSegment StartX=-8.5 StartY=-4.3 StartZ=0 EndX=-8.5 EndY=-33.9 EndZ=0
    g18: LineSegment StartX=-5.5 StartY=-10.5 StartZ=0 EndX=-5.5 EndY=-27.7 EndZ=0
    g19: LineSegment StartX=-11.5 StartY=-4.3 StartZ=0 EndX=-11.5 EndY=-33.9 EndZ=0
    g20: LineSegment StartX=-14.6 StartY=-1.8 StartZ=0 EndX=-14.6 EndY=-36.4 EndZ=0
    g21: LineSegment StartX=-17.6 StartY=-1.8 StartZ=0 EndX=-17.6 EndY=-36.4 EndZ=0
    g22: LineSegment StartX=-20.6 StartY=-36.4 StartZ=0 EndX=-20.6 EndY=-1.8 EndZ=0
    g23: LineSegment StartX=-23.6 StartY=-1.8 StartZ=0 EndX=-23.6 EndY=-36.4 EndZ=0
  constraints (48):
    c: Block(g0)
    c: Block(g1)
    c: Block(g2)
    c: Block(g3)
    c: Block(g4)
    c: Block(g5)
    c: Block(g6)
    c: Block(g7)
    c: Block(g8)
    c: Block(g9)
    c: Block(g10)
    c: Block(g11)
    c: Coincident(g12,g1)
    c: Coincident(g12,g2)
    c: Vertical(g12)
    c: Coincident(g13,g1)
    c: Coincident(g13,g2)
    c: Vertical(g13)
    c: Coincident(g14,g11)
    c: Coincident(g14,g7)
    c: Vertical(g14)
    c: Coincident(g15,g11)
    c: Coincident(g15,g7)
    c: Vertical(g15)
    c: Coincident(g16,g0)
    c: Coincident(g16,g3)
    c: Vertical(g16)
    c: Coincident(g17,g4)
    c: Coincident(g17,g8)
    c: Vertical(g17)
    c: Coincident(g18,g0)
    c: Coincident(g18,g3)
    c: Vertical(g18)
    c: Coincident(g19,g4)
    c: Coincident(g19,g8)
    c: Vertical(g19)
    c: Coincident(g20,g5)
    c: Coincident(g20,g9)
    c: Vertical(g20)
    c: Coincident(g21,g5)
    c: Coincident(g21,g9)
    c: Vertical(g21)
    c: Coincident(g22,g10)
    c: Coincident(g22,g6)
    c: Vertical(g22)
    c: Coincident(g23,g6)
    c: Coincident(g23,g10)
    c: Vertical(g23)
FEATURE [Part::Extrusion] Extrude020  label="removeToCreateFanGrillHoles"
  Base = -> Sketch029
  Dir = (0,-1,6e-16)
  DirMode = 2
  FaceMakerClass = Part::FaceMakerBullseye
  LengthFwd = 10
  LengthRev = 0
  Placement = pos=(65.4,44,54.82) rot=(0,0,1;0rad)
  Solid = true
  Symmetric = false
FEATURE [Part::MultiFuse] Fusion055  label="top008"
  Shapes = -> [Cut017,Cut018]
FEATURE [Part::Cut] Cut019  label="top009"
  Base = -> Fusion055
  Tool = -> Extrude020
FEATURE [App::MeasureDistance] Distance003  label="Distance: 71.95 mm"
  Distance = 71.9513
  P1 = (117,38,72)
  P2 = (117,38,0.0487319)
FEATURE [Sketcher::SketchObject] Sketch030
  FullyConstrained = true
  Placement = pos=(117,19,0) rot=(0.57735,0.57735,0.57735;2.0944rad)
  sketch-geometry (48):
    g0: LineSegment StartX=-49.19 StartY=69.25 StartZ=0 EndX=-49.19 EndY=66.25 EndZ=0
    g1: LineSegment StartX=-49.19 StartY=63.5 StartZ=0 EndX=-49.19 EndY=60.5 EndZ=0
    g2: LineSegment StartX=-49.19 StartY=57.75 StartZ=0 EndX=-49.19 EndY=54.75 EndZ=0
    g3: LineSegment StartX=-49.19 StartY=52 StartZ=0 EndX=-49.19 EndY=49 EndZ=0
    g4: LineSegment StartX=-49.19 StartY=46.25 StartZ=0 EndX=-49.19 EndY=43.25 EndZ=0
    g5: LineSegment StartX=-49.19 StartY=40.5 StartZ=0 EndX=-49.19 EndY=37.5 EndZ=0
    g6: LineSegment StartX=-49.19 StartY=34.5 StartZ=0 EndX=-49.19 EndY=31.5 EndZ=0
    g7: LineSegment StartX=-49.19 StartY=28.75 StartZ=0 EndX=-49.19 EndY=25.75 EndZ=0
    g8: LineSegment StartX=-49.19 StartY=23 StartZ=0 EndX=-49.19 EndY=20 EndZ=0
    g9: LineSegment StartX=-49.19 StartY=17.25 StartZ=0 EndX=-49.19 EndY=14.25 EndZ=0
    g10: LineSegment StartX=-49.19 StartY=11.5 StartZ=0 EndX=-49.19 EndY=8.5 EndZ=0
    g11: LineSegment StartX=-49.19 StartY=5.75 StartZ=0 EndX=-49.19 EndY=2.75 EndZ=0
    g12: ArcOfCircle CenterX=-1.5 CenterY=67.75 CenterZ=0 NormalX=0 NormalY=0 NormalZ=1 AngleXU=0 Radius=1.5 StartAngle=4.71239 EndAngle=7.85398
    g13: ArcOfCircle CenterX=-1.5 CenterY=62 CenterZ=0 NormalX=0 NormalY=0 NormalZ=1 AngleXU=0 Radius=1.5 StartAngle=4.71239 EndAngle=7.85398
    g14: ArcOfCircle CenterX=-1.5 CenterY=56.25 CenterZ=0 NormalX=0 NormalY=0 NormalZ=1 AngleXU=0 Radius=1.5 StartAngle=4.71239 EndAngle=7.85398
    g15: ArcOfCircle CenterX=-11.49 CenterY=50.5 CenterZ=0 NormalX=0 NormalY=0 NormalZ=1 AngleXU=0 Radius=1.5 StartAngle=4.71239 EndAngle=7.85398
    g16: ArcOfCircle CenterX=-16.28 CenterY=44.75 CenterZ=0 NormalX=0 NormalY=0 NormalZ=1 AngleXU=0 Radius=1.5 StartAngle=4.71239 EndAngle=7.85398
    g17: ArcOfCircle CenterX=-18.2337 CenterY=39 CenterZ=0 NormalX=0 NormalY=0 NormalZ=1 AngleXU=0 Radius=1.5 StartAngle=4.71485 EndAngle=7.85398
    g18: ArcOfCircle CenterX=-16.2837 CenterY=27.25 CenterZ=0 NormalX=0 NormalY=0 NormalZ=1 AngleXU=0 Radius=1.5 StartAngle=4.71485 EndAngle=7.85398
    g19: ArcOfCircle CenterX=-18.2337 CenterY=33 CenterZ=0 NormalX=0 NormalY=0 NormalZ=1 AngleXU=0 Radius=1.5 StartAngle=4.71485 EndAngle=7.85398
    g20: ArcOfCircle CenterX=-11.49 CenterY=21.5 CenterZ=0 NormalX=0 NormalY=0 NormalZ=1 AngleXU=0 Radius=1.5 StartAngle=4.71239 EndAngle=7.85398
    g21: ArcOfCircle CenterX=-1.5 CenterY=4.25 CenterZ=0 NormalX=0 NormalY=0 NormalZ=1 AngleXU=0 Radius=1.5 StartAngle=4.71239 EndAngle=7.85398
    g22: ArcOfCircle CenterX=-1.5 CenterY=10 CenterZ=0 NormalX=0 NormalY=0 NormalZ=1 AngleXU=0 Radius=1.5 StartAngle=4.71239 EndAngle=7.85398
    g23: ArcOfCircle CenterX=-1.5 CenterY=15.75 CenterZ=0 NormalX=0 NormalY=0 NormalZ=1 AngleXU=0 Radius=1.5 StartAngle=4.71239 EndAngle=7.85398
    g24: LineSegment StartX=-49.19 StartY=69.25 StartZ=0 EndX=-1.5 EndY=69.25 EndZ=0
    g25: LineSegment StartX=-49.19 StartY=66.25 StartZ=0 EndX=-1.5 EndY=66.25 EndZ=0
    g26: LineSegment StartX=-49.19 StartY=63.5 StartZ=0 EndX=-1.5 EndY=63.5 EndZ=0
    g27: LineSegment StartX=-49.19 StartY=60.5 StartZ=0 EndX=-1.5 EndY=60.5 EndZ=0
    g28: LineSegment StartX=-49.19 StartY=57.75 StartZ=0 EndX=-1.5 EndY=57.75 EndZ=0
    g29: LineSegment StartX=-49.19 StartY=54.75 StartZ=0 EndX=-1.5 EndY=54.75 EndZ=0
    g30: LineSegment StartX=-49.19 StartY=52 StartZ=0 EndX=-11.49 EndY=52 EndZ=0
    g31: LineSegment StartX=-49.19 StartY=49 StartZ=0 EndX=-11.49 EndY=49 EndZ=0
    g32: LineSegment StartX=-49.19 StartY=46.25 StartZ=0 EndX=-16.28 EndY=46.25 EndZ=0
    g33: LineSegment StartX=-49.19 StartY=43.25 StartZ=0 EndX=-16.28 EndY=43.25 EndZ=0
    g34: LineSegment StartX=-49.19 StartY=40.5 StartZ=0 EndX=-18.2337 EndY=40.5 EndZ=0
    g35: LineSegment StartX=-49.19 StartY=37.5 StartZ=0 EndX=-18.23 EndY=37.5 EndZ=0
    g36: LineSegment StartX=-49.19 StartY=34.5 StartZ=0 EndX=-18.2337 EndY=34.5 EndZ=0
    g37: LineSegment StartX=-49.19 StartY=31.5 StartZ=0 EndX=-18.23 EndY=31.5 EndZ=0
    g38: LineSegment StartX=-49.19 StartY=28.75 StartZ=0 EndX=-16.2837 EndY=28.75 EndZ=0
    g39: LineSegment StartX=-49.19 StartY=25.75 StartZ=0 EndX=-16.28 EndY=25.75 EndZ=0
    g40: LineSegment StartX=-49.19 StartY=23 StartZ=0 EndX=-11.49 EndY=23 EndZ=0
    g41: LineSegment StartX=-49.19 StartY=20 StartZ=0 EndX=-11.49 EndY=20 EndZ=0
    g42: LineSegment StartX=-49.19 StartY=17.25 StartZ=0 EndX=-1.5 EndY=17.25 EndZ=0
    g43: LineSegment StartX=-49.19 StartY=14.25 StartZ=0 EndX=-1.5 EndY=14.25 EndZ=0
    g44: LineSegment StartX=-49.19 StartY=11.5 StartZ=0 EndX=-1.5 EndY=11.5 EndZ=0
    g45: LineSegment StartX=-49.19 StartY=8.5 StartZ=0 EndX=-1.5 EndY=8.5 EndZ=0
    g46: LineSegment StartX=-49.19 StartY=5.75 StartZ=0 EndX=-1.5 EndY=5.75 EndZ=0
    g47: LineSegment StartX=-49.19 StartY=2.75 StartZ=0 EndX=-1.5 EndY=2.75 EndZ=0
  constraints (120):
    c: Vertical(g0)
    c: Distance(g0) = 3
    c: Block(g0)
    c: Vertical(g1)
    c: Distance(g1) = 3
    c: Vertical(g2)
    c: Equal(g0,g2) = 3
    c: Block(g2)
    c: Vertical(g3)
    c: Equal(g1,g3) = 3
    c: Vertical(g4)
    c: Equal(g0,g4) = 3
    c: Block(g4)
    c: Vertical(g5)
    c: Equal(g1,g5) = 3
    c: Vertical(g6)
    c: Equal(g0,g6) = 3
    c: Block(g6)
    c: Vertical(g7)
    c: Equal(g1,g7) = 3
    c: Vertical(g8)
    c: Equal(g0,g8) = 3
    c: Block(g8)
    c: Vertical(g9)
    c: Equal(g1,g9) = 3
    c: Vertical(g10)
    c: Equal(g0,g10) = 3
    c: Block(g10)
    c: Vertical(g11)
    c: Equal(g1,g11) = 3
    c: Block(g12)
    c: Block(g13)
    c: Block(g14)
    c: Block(g15)
    c: Block(g16)
    c: Block(g17)
    c: Block(g18)
    c: Block(g19)
    c: Block(g20)
    c: Block(g21)
    c: Block(g22)
    c: Block(g23)
    c: Block(g11)
    c: Block(g9)
    c: Block(g7)
    c: Block(g5)
    c: Block(g3)
    c: Block(g1)
    c: Coincident(g24,g0)
    c: Coincident(g24,g12)
    c: Horizontal(g24)
    c: Coincident(g25,g0)
    c: Coincident(g25,g12)
    c: Horizontal(g25)
    c: Coincident(g26,g1)
    c: Coincident(g26,g13)
    c: Horizontal(g26)
    c: Coincident(g27,g1)
    c: Coincident(g27,g13)
    c: Horizontal(g27)
    c: Coincident(g28,g2)
    c: Coincident(g28,g14)
    c: Horizontal(g28)
    c: Coincident(g29,g2)
    c: Coincident(g29,g14)
    c: Horizontal(g29)
    c: Coincident(g30,g3)
    c: Coincident(g30,g15)
    c: Horizontal(g30)
    c: Coincident(g31,g3)
    c: Coincident(g31,g15)
    c: Horizontal(g31)
    c: Coincident(g32,g4)
    c: Coincident(g32,g16)
    c: Horizontal(g32)
    c: Coincident(g33,g4)
    c: Coincident(g33,g16)
    c: Horizontal(g33)
    c: Coincident(g34,g5)
    c: Coincident(g34,g17)
    c: Horizontal(g34)
    c: Coincident(g35,g5)
    c: Coincident(g35,g17)
    c: Horizontal(g35)
    c: Coincident(g36,g6)
    c: Coincident(g36,g19)
    c: Horizontal(g36)
    c: Coincident(g37,g6)
    c: Coincident(g37,g19)
    c: Horizontal(g37)
    c: Coincident(g38,g7)
    c: Coincident(g38,g18)
    c: Horizontal(g38)
    c: Coincident(g39,g7)
    c: Coincident(g39,g18)
    c: Horizontal(g39)
    c: Coincident(g40,g8)
    c: Coincident(g40,g20)
    c: Horizontal(g40)
    c: Coincident(g41,g8)
    c: Coincident(g41,g20)
    c: Horizontal(g41)
    c: Coincident(g42,g9)
    c: Coincident(g42,g23)
    c: Horizontal(g42)
    c: Coincident(g43,g9)
    c: Coincident(g43,g23)
    c: Horizontal(g43)
    c: Coincident(g44,g10)
    c: Coincident(g44,g22)
    c: Horizontal(g44)
    c: Coincident(g45,g10)
    c: Coincident(g45,g22)
    c: Horizontal(g45)
    c: Coincident(g46,g11)
    c: Coincident(g46,g21)
    c: Horizontal(g46)
    c: Coincident(g47,g11)
    c: Coincident(g47,g21)
    c: Horizontal(g47)
FEATURE [Sketcher::SketchObject] Sketch031
  FullyConstrained = true
  Placement = pos=(117,19,0) rot=(0.57735,0.57735,0.57735;2.0944rad)
  sketch-geometry (24):
    g0: ArcOfCircle CenterX=-49.19 CenterY=67.75 CenterZ=0 NormalX=0 NormalY=0 NormalZ=1 AngleXU=0 Radius=1.5 StartAngle=1.5708 EndAngle=4.71239
    g1: ArcOfCircle CenterX=-49.19 CenterY=62 CenterZ=0 NormalX=0 NormalY=0 NormalZ=1 AngleXU=0 Radius=1.5 StartAngle=1.5708 EndAngle=4.71239
    g2: ArcOfCircle CenterX=-49.19 CenterY=56.25 CenterZ=0 NormalX=0 NormalY=0 NormalZ=1 AngleXU=0 Radius=1.5 StartAngle=1.5708 EndAngle=4.71239
    g3: ArcOfCircle CenterX=-49.19 CenterY=50.5 CenterZ=0 NormalX=0 NormalY=0 NormalZ=1 AngleXU=0 Radius=1.5 StartAngle=1.5708 EndAngle=4.71239
    g4: ArcOfCircle CenterX=-49.19 CenterY=44.75 CenterZ=0 NormalX=0 NormalY=0 NormalZ=1 AngleXU=0 Radius=1.5 StartAngle=1.5708 EndAngle=4.71239
    g5: ArcOfCircle CenterX=-49.19 CenterY=39 CenterZ=0 NormalX=0 NormalY=0 NormalZ=1 AngleXU=0 Radius=1.5 StartAngle=1.5708 EndAngle=4.71239
    g6: ArcOfCircle CenterX=-49.19 CenterY=33 CenterZ=0 NormalX=0 NormalY=0 NormalZ=1 AngleXU=0 Radius=1.5 StartAngle=1.5708 EndAngle=4.71239
    g7: ArcOfCircle CenterX=-49.19 CenterY=27.25 CenterZ=0 NormalX=0 NormalY=0 NormalZ=1 AngleXU=0 Radius=1.5 StartAngle=1.5708 EndAngle=4.71239
    g8: ArcOfCircle CenterX=-49.19 CenterY=21.5 CenterZ=0 NormalX=0 NormalY=0 NormalZ=1 AngleXU=0 Radius=1.5 StartAngle=1.5708 EndAngle=4.71239
    g9: ArcOfCircle CenterX=-49.19 CenterY=15.75 CenterZ=0 NormalX=0 NormalY=0 NormalZ=1 AngleXU=0 Radius=1.5 StartAngle=1.5708 EndAngle=4.71239
    g10: ArcOfCircle CenterX=-49.19 CenterY=10 CenterZ=0 NormalX=0 NormalY=0 NormalZ=1 AngleXU=0 Radius=1.5 StartAngle=1.5708 EndAngle=4.71239
    g11: ArcOfCircle CenterX=-49.19 CenterY=4.25 CenterZ=0 NormalX=0 NormalY=0 NormalZ=1 AngleXU=0 Radius=1.5 StartAngle=1.5708 EndAngle=4.71239
    g12: LineSegment StartX=-49.19 StartY=69.25 StartZ=0 EndX=-49.19 EndY=66.25 EndZ=0
    g13: LineSegment StartX=-49.19 StartY=63.5 StartZ=0 EndX=-49.19 EndY=60.5 EndZ=0
    g14: LineSegment StartX=-49.19 StartY=57.75 StartZ=0 EndX=-49.19 EndY=54.75 EndZ=0
    g15: LineSegment StartX=-49.19 StartY=52 StartZ=0 EndX=-49.19 EndY=49 EndZ=0
    g16: LineSegment StartX=-49.19 StartY=46.25 StartZ=0 EndX=-49.19 EndY=43.25 EndZ=0
    g17: LineSegment StartX=-49.19 StartY=40.5 StartZ=0 EndX=-49.19 EndY=37.5 EndZ=0
    g18: LineSegment StartX=-49.19 StartY=34.5 StartZ=0 EndX=-49.19 EndY=31.5 EndZ=0
    g19: LineSegment StartX=-49.19 StartY=28.75 StartZ=0 EndX=-49.19 EndY=25.75 EndZ=0
    g20: LineSegment StartX=-49.19 StartY=23 StartZ=0 EndX=-49.19 EndY=20 EndZ=0
    g21: LineSegment StartX=-49.19 StartY=17.25 StartZ=0 EndX=-49.19 EndY=14.25 EndZ=0
    g22: LineSegment StartX=-49.19 StartY=11.5 StartZ=0 EndX=-49.19 EndY=8.5 EndZ=0
    g23: LineSegment StartX=-49.19 StartY=5.75 StartZ=0 EndX=-49.19 EndY=2.75 EndZ=0
  constraints (48):
    c: Block(g0)
    c: Block(g1)
    c: Block(g2)
    c: Block(g3)
    c: Block(g4)
    c: Block(g5)
    c: Block(g6)
    c: Block(g7)
    c: Block(g8)
    c: Block(g9)
    c: Block(g10)
    c: Block(g11)
    c: Coincident(g12,g0)
    c: Coincident(g12,g0)
    c: Vertical(g12)
    c: Vertical(g13)
    c: Coincident(g13,g1)
    c: Vertical(g14)
    c: Coincident(g14,g2)
    c: Vertical(g15)
    c: Coincident(g15,g3)
    c: Vertical(g16)
    c: Coincident(g16,g4)
    c: Vertical(g17)
    c: Coincident(g17,g5)
    c: Vertical(g18)
    c: Coincident(g18,g6)
    c: Vertical(g19)
    c: Coincident(g19,g7)
    c: Vertical(g20)
    c: Coincident(g20,g8)
    c: Vertical(g21)
    c: Coincident(g21,g9)
    c: Vertical(g22)
    c: Coincident(g22,g10)
    c: Vertical(g23)
    c: Coincident(g23,g11)
    c: Block(g23)
    c: Block(g22)
    c: Block(g21)
    c: Block(g20)
    c: Block(g13)
    c: Block(g14)
    c: Block(g15)
    c: Block(g16)
    c: Block(g17)
    c: Block(g18)
    c: Block(g19)
FEATURE [Part::Extrusion] Extrude022
  Base = -> Sketch030
  Dir = (1,-2e-16,2e-16)
  DirMode = 2
  FaceMakerClass = Part::FaceMakerBullseye
  LengthFwd = 19
  LengthRev = 0
  Placement = pos=(-19,0,0) rot=(0,0,1;0rad)
  Solid = true
  Symmetric = false
FEATURE [Part::Fillet] Fillet022
  Base = -> Extrude022
  Edges = 24 edges r=1.49: [Edge6,Edge11,Edge18,Edge23,Edge30,Edge35,Edge42,Edge47,Edge54,Edge59,Edge66,Edge71,Edge78,Edge83,Edge90,Edge95,Edge102,Edge107,Edge114,Edge119,Edge126,Edge131,Edge138,Edge143]
FEATURE [Part::Cut] Cut020  label="top010"
  Base = -> Cut019
  Tool = -> Fillet022
FEATURE [Sketcher::SketchObject] Sketch032
  FullyConstrained = true
  Placement = pos=(117,19,0) rot=(0.57735,0.57735,0.57735;2.0944rad)
  sketch-geometry (48):
    g0: LineSegment StartX=-49.19 StartY=69.25 StartZ=0 EndX=-49.19 EndY=66.25 EndZ=0
    g1: LineSegment StartX=-49.19 StartY=63.5 StartZ=0 EndX=-49.19 EndY=60.5 EndZ=0
    g2: LineSegment StartX=-49.19 StartY=57.75 StartZ=0 EndX=-49.19 EndY=54.75 EndZ=0
    g3: LineSegment StartX=-49.19 StartY=52 StartZ=0 EndX=-49.19 EndY=49 EndZ=0
    g4: LineSegment StartX=-49.19 StartY=46.25 StartZ=0 EndX=-49.19 EndY=43.25 EndZ=0
    g5: LineSegment StartX=-49.19 StartY=40.5 StartZ=0 EndX=-49.19 EndY=37.5 EndZ=0
    g6: LineSegment StartX=-49.19 StartY=34.5 StartZ=0 EndX=-49.19 EndY=31.5 EndZ=0
    g7: LineSegment StartX=-49.19 StartY=28.75 StartZ=0 EndX=-49.19 EndY=25.75 EndZ=0
    g8: LineSegment StartX=-49.19 StartY=23 StartZ=0 EndX=-49.19 EndY=20 EndZ=0
    g9: LineSegment StartX=-49.19 StartY=17.25 StartZ=0 EndX=-49.19 EndY=14.25 EndZ=0
    g10: LineSegment StartX=-49.19 StartY=11.5 StartZ=0 EndX=-49.19 EndY=8.5 EndZ=0
    g11: LineSegment StartX=-49.19 StartY=5.75 StartZ=0 EndX=-49.19 EndY=2.75 EndZ=0
    g12: ArcOfCircle CenterX=-1.5 CenterY=67.75 CenterZ=0 NormalX=0 NormalY=0 NormalZ=1 AngleXU=0 Radius=1.5 StartAngle=4.71239 EndAngle=7.85398
    g13: ArcOfCircle CenterX=-1.5 CenterY=62 CenterZ=0 NormalX=0 NormalY=0 NormalZ=1 AngleXU=0 Radius=1.5 StartAngle=4.71239 EndAngle=7.85398
    g14: ArcOfCircle CenterX=-1.5 CenterY=56.25 CenterZ=0 NormalX=0 NormalY=0 NormalZ=1 AngleXU=0 Radius=1.5 StartAngle=4.71239 EndAngle=7.85398
    g15: ArcOfCircle CenterX=-11.49 CenterY=50.5 CenterZ=0 NormalX=0 NormalY=0 NormalZ=1 AngleXU=0 Radius=1.5 StartAngle=4.71239 EndAngle=7.85398
    g16: ArcOfCircle CenterX=-16.28 CenterY=44.75 CenterZ=0 NormalX=0 NormalY=0 NormalZ=1 AngleXU=0 Radius=1.5 StartAngle=4.71239 EndAngle=7.85398
    g17: ArcOfCircle CenterX=-18.2337 CenterY=39 CenterZ=0 NormalX=0 NormalY=0 NormalZ=1 AngleXU=0 Radius=1.5 StartAngle=4.71485 EndAngle=7.85398
    g18: ArcOfCircle CenterX=-16.2837 CenterY=27.25 CenterZ=0 NormalX=0 NormalY=0 NormalZ=1 AngleXU=0 Radius=1.5 StartAngle=4.71485 EndAngle=7.85398
    g19: ArcOfCircle CenterX=-18.2337 CenterY=33 CenterZ=0 NormalX=0 NormalY=0 NormalZ=1 AngleXU=0 Radius=1.5 StartAngle=4.71485 EndAngle=7.85398
    g20: ArcOfCircle CenterX=-11.49 CenterY=21.5 CenterZ=0 NormalX=0 NormalY=0 NormalZ=1 AngleXU=0 Radius=1.5 StartAngle=4.71239 EndAngle=7.85398
    g21: ArcOfCircle CenterX=-1.5 CenterY=4.25 CenterZ=0 NormalX=0 NormalY=0 NormalZ=1 AngleXU=0 Radius=1.5 StartAngle=4.71239 EndAngle=7.85398
    g22: ArcOfCircle CenterX=-1.5 CenterY=10 CenterZ=0 NormalX=0 NormalY=0 NormalZ=1 AngleXU=0 Radius=1.5 StartAngle=4.71239 EndAngle=7.85398
    g23: ArcOfCircle CenterX=-1.5 CenterY=15.75 CenterZ=0 NormalX=0 NormalY=0 NormalZ=1 AngleXU=0 Radius=1.5 StartAngle=4.71239 EndAngle=7.85398
    g24: LineSegment StartX=-49.19 StartY=69.25 StartZ=0 EndX=-1.5 EndY=69.25 EndZ=0
    g25: LineSegment StartX=-49.19 StartY=66.25 StartZ=0 EndX=-1.5 EndY=66.25 EndZ=0
    g26: LineSegment StartX=-49.19 StartY=63.5 StartZ=0 EndX=-1.5 EndY=63.5 EndZ=0
    g27: LineSegment StartX=-49.19 StartY=60.5 StartZ=0 EndX=-1.5 EndY=60.5 EndZ=0
    g28: LineSegment StartX=-49.19 StartY=57.75 StartZ=0 EndX=-1.5 EndY=57.75 EndZ=0
    g29: LineSegment StartX=-49.19 StartY=54.75 StartZ=0 EndX=-1.5 EndY=54.75 EndZ=0
    g30: LineSegment StartX=-49.19 StartY=52 StartZ=0 EndX=-11.49 EndY=52 EndZ=0
    g31: LineSegment StartX=-49.19 StartY=49 StartZ=0 EndX=-11.49 EndY=49 EndZ=0
    g32: LineSegment StartX=-49.19 StartY=46.25 StartZ=0 EndX=-16.28 EndY=46.25 EndZ=0
    g33: LineSegment StartX=-49.19 StartY=43.25 StartZ=0 EndX=-16.28 EndY=43.25 EndZ=0
    g34: LineSegment StartX=-49.19 StartY=40.5 StartZ=0 EndX=-18.2337 EndY=40.5 EndZ=0
    g35: LineSegment StartX=-49.19 StartY=37.5 StartZ=0 EndX=-18.23 EndY=37.5 EndZ=0
    g36: LineSegment StartX=-49.19 StartY=34.5 StartZ=0 EndX=-18.2337 EndY=34.5 EndZ=0
    g37: LineSegment StartX=-49.19 StartY=31.5 StartZ=0 EndX=-18.23 EndY=31.5 EndZ=0
    g38: LineSegment StartX=-49.19 StartY=28.75 StartZ=0 EndX=-16.2837 EndY=28.75 EndZ=0
    g39: LineSegment StartX=-49.19 StartY=25.75 StartZ=0 EndX=-16.28 EndY=25.75 EndZ=0
    g40: LineSegment StartX=-49.19 StartY=23 StartZ=0 EndX=-11.49 EndY=23 EndZ=0
    g41: LineSegment StartX=-49.19 StartY=20 StartZ=0 EndX=-11.49 EndY=20 EndZ=0
    g42: LineSegment StartX=-49.19 StartY=17.25 StartZ=0 EndX=-1.5 EndY=17.25 EndZ=0
    g43: LineSegment StartX=-49.19 StartY=14.25 StartZ=0 EndX=-1.5 EndY=14.25 EndZ=0
    g44: LineSegment StartX=-49.19 StartY=11.5 StartZ=0 EndX=-1.5 EndY=11.5 EndZ=0
    g45: LineSegment StartX=-49.19 StartY=8.5 StartZ=0 EndX=-1.5 EndY=8.5 EndZ=0
    g46: LineSegment StartX=-49.19 StartY=5.75 StartZ=0 EndX=-1.5 EndY=5.75 EndZ=0
    g47: LineSegment StartX=-49.19 StartY=2.75 StartZ=0 EndX=-1.5 EndY=2.75 EndZ=0
  constraints (120):
    c: Vertical(g0)
    c: Distance(g0) = 3
    c: Block(g0)
    c: Vertical(g1)
    c: Distance(g1) = 3
    c: Vertical(g2)
    c: Equal(g0,g2) = 3
    c: Block(g2)
    c: Vertical(g3)
    c: Equal(g1,g3) = 3
    c: Vertical(g4)
    c: Equal(g0,g4) = 3
    c: Block(g4)
    c: Vertical(g5)
    c: Equal(g1,g5) = 3
    c: Vertical(g6)
    c: Equal(g0,g6) = 3
    c: Block(g6)
    c: Vertical(g7)
    c: Equal(g1,g7) = 3
    c: Vertical(g8)
    c: Equal(g0,g8) = 3
    c: Block(g8)
    c: Vertical(g9)
    c: Equal(g1,g9) = 3
    c: Vertical(g10)
    c: Equal(g0,g10) = 3
    c: Block(g10)
    c: Vertical(g11)
    c: Equal(g1,g11) = 3
    c: Block(g12)
    c: Block(g13)
    c: Block(g14)
    c: Block(g15)
    c: Block(g16)
    c: Block(g17)
    c: Block(g18)
    c: Block(g19)
    c: Block(g20)
    c: Block(g21)
    c: Block(g22)
    c: Block(g23)
    c: Block(g11)
    c: Block(g9)
    c: Block(g7)
    c: Block(g5)
    c: Block(g3)
    c: Block(g1)
    c: Coincident(g24,g0)
    c: Coincident(g24,g12)
    c: Horizontal(g24)
    c: Coincident(g25,g0)
    c: Coincident(g25,g12)
    c: Horizontal(g25)
    c: Coincident(g26,g1)
    c: Coincident(g26,g13)
    c: Horizontal(g26)
    c: Coincident(g27,g1)
    c: Coincident(g27,g13)
    c: Horizontal(g27)
    c: Coincident(g28,g2)
    c: Coincident(g28,g14)
    c: Horizontal(g28)
    c: Coincident(g29,g2)
    c: Coincident(g29,g14)
    c: Horizontal(g29)
    c: Coincident(g30,g3)
    c: Coincident(g30,g15)
    c: Horizontal(g30)
    c: Coincident(g31,g3)
    c: Coincident(g31,g15)
    c: Horizontal(g31)
    c: Coincident(g32,g4)
    c: Coincident(g32,g16)
    c: Horizontal(g32)
    c: Coincident(g33,g4)
    c: Coincident(g33,g16)
    c: Horizontal(g33)
    c: Coincident(g34,g5)
    c: Coincident(g34,g17)
    c: Horizontal(g34)
    c: Coincident(g35,g5)
    c: Coincident(g35,g17)
    c: Horizontal(g35)
    c: Coincident(g36,g6)
    c: Coincident(g36,g19)
    c: Horizontal(g36)
    c: Coincident(g37,g6)
    c: Coincident(g37,g19)
    c: Horizontal(g37)
    c: Coincident(g38,g7)
    c: Coincident(g38,g18)
    c: Horizontal(g38)
    c: Coincident(g39,g7)
    c: Coincident(g39,g18)
    c: Horizontal(g39)
    c: Coincident(g40,g8)
    c: Coincident(g40,g20)
    c: Horizontal(g40)
    c: Coincident(g41,g8)
    c: Coincident(g41,g20)
    c: Horizontal(g41)
    c: Coincident(g42,g9)
    c: Coincident(g42,g23)
    c: Horizontal(g42)
    c: Coincident(g43,g9)
    c: Coincident(g43,g23)
    c: Horizontal(g43)
    c: Coincident(g44,g10)
    c: Coincident(g44,g22)
    c: Horizontal(g44)
    c: Coincident(g45,g10)
    c: Coincident(g45,g22)
    c: Horizontal(g45)
    c: Coincident(g46,g11)
    c: Coincident(g46,g21)
    c: Horizontal(g46)
    c: Coincident(g47,g11)
    c: Coincident(g47,g21)
    c: Horizontal(g47)
FEATURE [Part::Extrusion] Extrude023
  Base = -> Sketch032
  Dir = (1,-2e-16,2e-16)
  DirMode = 2
  FaceMakerClass = Part::FaceMakerBullseye
  LengthFwd = 19
  LengthRev = 0
  Placement = pos=(-19,0,0) rot=(0,0,1;0rad)
  Solid = true
  Symmetric = false
FEATURE [Part::Fillet] Fillet023
  Base = -> Extrude023
  Edges = 24 edges r=1.49: [Edge6,Edge11,Edge18,Edge23,Edge30,Edge35,Edge42,Edge47,Edge54,Edge59,Edge66,Edge71,Edge78,Edge83,Edge90,Edge95,Edge102,Edge107,Edge114,Edge119,Edge126,Edge131,Edge138,Edge143]
  Placement = pos=(0,0.05,0) rot=(0,0,1;0rad)
FEATURE [Part::Cut] Cut014  label="bottom003"
  Base = -> Cut007
  Tool = -> Fusion047
FEATURE [Part::Cut] Cut021  label="bottom004"
  Base = -> Cut014
  Tool = -> Fillet023
FEATURE [Sketcher::SketchObject] Sketch033
  FullyConstrained = true
  Placement = pos=(117,19,0) rot=(0.57735,0.57735,0.57735;2.0944rad)
  sketch-geometry (8):
    g0: LineSegment StartX=-49.19 StartY=69.25 StartZ=0 EndX=-49.19 EndY=66.25 EndZ=0
    g1: LineSegment StartX=-49.19 StartY=5.75 StartZ=0 EndX=-49.19 EndY=2.75 EndZ=0
    g2: ArcOfCircle CenterX=-1.5 CenterY=67.75 CenterZ=0 NormalX=0 NormalY=0 NormalZ=1 AngleXU=0 Radius=1.5 StartAngle=4.71239 EndAngle=7.85398
    g3: ArcOfCircle CenterX=-1.5 CenterY=4.25 CenterZ=0 NormalX=0 NormalY=0 NormalZ=1 AngleXU=0 Radius=1.5 StartAngle=4.71239 EndAngle=7.85398
    g4: LineSegment StartX=-49.19 StartY=69.25 StartZ=0 EndX=-1.5 EndY=69.25 EndZ=0
    g5: LineSegment StartX=-49.19 StartY=66.25 StartZ=0 EndX=-1.5 EndY=66.25 EndZ=0
    g6: LineSegment StartX=-49.19 StartY=5.75 StartZ=0 EndX=-1.5 EndY=5.75 EndZ=0
    g7: LineSegment StartX=-49.19 StartY=2.75 StartZ=0 EndX=-1.5 EndY=2.75 EndZ=0
  constraints (19):
    c: Vertical(g0)
    c: Distance(g0) = 3
    c: Block(g0)
    c: Vertical(g1)
    c: Block(g2)
    c: Block(g3)
    c: Block(g1)
    c: Coincident(g4,g0)
    c: Coincident(g4,g2)
    c: Horizontal(g4)
    c: Coincident(g5,g0)
    c: Coincident(g5,g2)
    c: Horizontal(g5)
    c: Coincident(g6,g1)
    c: Coincident(g6,g3)
    c: Horizontal(g6)
    c: Coincident(g7,g1)
    c: Coincident(g7,g3)
    c: Horizontal(g7)
FEATURE [Sketcher::SketchObject] Sketch034
  FullyConstrained = true
  Placement = pos=(117,19,0) rot=(0.57735,0.57735,0.57735;2.0944rad)
  sketch-geometry (8):
    g0: LineSegment StartX=-49.19 StartY=63.5 StartZ=0 EndX=-49.19 EndY=60.5 EndZ=0
    g1: LineSegment StartX=-49.19 StartY=11.5 StartZ=0 EndX=-49.19 EndY=8.5 EndZ=0
    g2: ArcOfCircle CenterX=-1.5 CenterY=62 CenterZ=0 NormalX=0 NormalY=0 NormalZ=1 AngleXU=0 Radius=1.5 StartAngle=4.71239 EndAngle=7.85398
    g3: ArcOfCircle CenterX=-1.5 CenterY=10 CenterZ=0 NormalX=0 NormalY=0 NormalZ=1 AngleXU=0 Radius=1.5 StartAngle=4.71239 EndAngle=7.85398
    g4: LineSegment StartX=-49.19 StartY=63.5 StartZ=0 EndX=-1.5 EndY=63.5 EndZ=0
    g5: LineSegment StartX=-49.19 StartY=60.5 StartZ=0 EndX=-1.5 EndY=60.5 EndZ=0
    g6: LineSegment StartX=-49.19 StartY=11.5 StartZ=0 EndX=-1.5 EndY=11.5 EndZ=0
    g7: LineSegment StartX=-49.19 StartY=8.5 StartZ=0 EndX=-1.5 EndY=8.5 EndZ=0
  constraints (19):
    c: Vertical(g0)
    c: Distance(g0) = 3
    c: Vertical(g1)
    c: Block(g1)
    c: Block(g2)
    c: Block(g3)
    c: Block(g0)
    c: Coincident(g4,g0)
    c: Coincident(g4,g2)
    c: Horizontal(g4)
    c: Coincident(g5,g0)
    c: Coincident(g5,g2)
    c: Horizontal(g5)
    c: Coincident(g6,g1)
    c: Coincident(g6,g3)
    c: Horizontal(g6)
    c: Coincident(g7,g1)
    c: Coincident(g7,g3)
    c: Horizontal(g7)
FEATURE [Part::Extrusion] Extrude024
  Base = -> Sketch033
  Dir = (1,0,0)
  DirMode = 2
  FaceMakerClass = Part::FaceMakerBullseye
  LengthFwd = 10
  LengthRev = 0
  Solid = true
  Symmetric = false
FEATURE [Part::Extrusion] Extrude025
  Base = -> Sketch034
  Dir = (1,0,0)
  DirMode = 2
  FaceMakerClass = Part::FaceMakerBullseye
  LengthFwd = 10
  LengthRev = 0
  Solid = true
  Symmetric = false
FEATURE [Part::Fillet] Fillet024  label="removeFromtMoreFrontCaseScrewRetainers"
  Base = -> Extrude024
  Edges = 4 edges r=1.49: [Edge6,Edge11,Edge18,Edge23]
  Placement = pos=(-11,0,0) rot=(0,0,1;0rad)
FEATURE [Part::Fillet] Fillet025  label="removeFromtMoreFrontCaseScrewRetainers001"
  Base = -> Extrude025
  Edges = 4 edges r=1.49: [Edge6,Edge11,Edge18,Edge23]
  Placement = pos=(-19,0,0) rot=(0,0,1;0rad)
FEATURE [Part::Cut] Cut022
  Base = -> Cut015
  Tool = -> Fillet025
FEATURE [Part::Cut] Cut023  label="screwRetainers"
  Base = -> Cut022
  Tool = -> Fillet024
FEATURE [Part::MultiFuse] Fusion056  label="bottom005"
  Shapes = -> [Fusion044,Cut021]
FEATURE [Part::MultiFuse] Fusion057  label="casePillars001"
  Shapes = -> [Cut016,Fusion052]
FEATURE [Part::MultiFuse] Fusion058  label="bottom006"
  Shapes = -> [Fusion056,Cut023]
FEATURE [Part::MultiFuse] Fusion059  label="bottom007"
  Shapes = -> [Fusion058,Fillet005]
FEATURE [Part::MultiFuse] Fusion060  label="bottom008"
  Shapes = -> [Fusion059,Fusion]
FEATURE [Part::MultiFuse] Fusion061  label="top011"
  Shapes = -> [Cut006,Cut020]
FEATURE [Part::MultiFuse] Fusion062  label="top012"
  Shapes = -> [Fusion057,Fusion061]
FEATURE [Sketcher::SketchObject] Sketch035  label="topSketch007"
  FullyConstrained = true
  sketch-geometry (6):
    g0: LineSegment StartX=19 StartY=38 StartZ=0 EndX=117 EndY=38 EndZ=0
    g1: ArcOfCircle CenterX=19 CenterY=19 CenterZ=0 NormalX=0 NormalY=0 NormalZ=1 AngleXU=0 Radius=19 StartAngle=1.5708 EndAngle=3.14159
    g2: LineSegment StartX=117 StartY=38 StartZ=0 EndX=117 EndY=19 EndZ=0
    g3: LineSegment StartX=98 StartY=1.0161e-12 StartZ=0 EndX=5.22862e-06 EndY=1.0161e-12 EndZ=0
    g4: LineSegment StartX=5.22862e-06 StartY=19 StartZ=0 EndX=5.22862e-06 EndY=1.0161e-12 EndZ=0
    g5: ArcOfCircle CenterX=98 CenterY=19 CenterZ=0 NormalX=0 NormalY=0 NormalZ=1 AngleXU=0 Radius=19 StartAngle=4.71239 EndAngle=6.28319
  constraints (16):
    c: Horizontal(g0)
    c: Distance(g0) = 98
    c: Coincident(g1,g0)
    c: Block(g1)
    c: Coincident(g2,g0)
    c: Vertical(g2)
    c: Distance(g2) = 19
    c: Horizontal(g3)
    c: Coincident(g4,g1)
    c: Vertical(g4)
    c: Coincident(g3,g4)
    c: Block(g3)
    c: Coincident(g5,g2)
    c: Coincident(g5,g3)
    c: Block(g0)
    c: Block(g5)
FEATURE [Part::Extrusion] Extrude026  label="sideA001"
  Base = -> Sketch035
  Dir = (0,0,1)
  DirMode = 2
  FaceMakerClass = Part::FaceMakerBullseye
  LengthFwd = 3
  LengthRev = 0
  Placement = pos=(0,0,-2.7) rot=(0,0,1;0rad)
  Solid = true
  Symmetric = false
FEATURE [Sketcher::SketchObject] Sketch036  label="topSketch008"
  FullyConstrained = true
  sketch-geometry (6):
    g0: LineSegment StartX=19 StartY=38 StartZ=0 EndX=117 EndY=38 EndZ=0
    g1: ArcOfCircle CenterX=19 CenterY=19 CenterZ=0 NormalX=0 NormalY=0 NormalZ=1 AngleXU=0 Radius=19 StartAngle=1.5708 EndAngle=3.14159
    g2: LineSegment StartX=117 StartY=38 StartZ=0 EndX=117 EndY=19 EndZ=0
    g3: LineSegment StartX=98 StartY=1.0161e-12 StartZ=0 EndX=5.22862e-06 EndY=1.0161e-12 EndZ=0
    g4: LineSegment StartX=5.22862e-06 StartY=19 StartZ=0 EndX=5.22862e-06 EndY=1.0161e-12 EndZ=0
    g5: ArcOfCircle CenterX=98 CenterY=19 CenterZ=0 NormalX=0 NormalY=0 NormalZ=1 AngleXU=0 Radius=19 StartAngle=4.71239 EndAngle=6.28319
  constraints (16):
    c: Horizontal(g0)
    c: Distance(g0) = 98
    c: Coincident(g1,g0)
    c: Block(g1)
    c: Coincident(g2,g0)
    c: Vertical(g2)
    c: Distance(g2) = 19
    c: Horizontal(g3)
    c: Coincident(g4,g1)
    c: Vertical(g4)
    c: Coincident(g3,g4)
    c: Block(g3)
    c: Coincident(g5,g2)
    c: Coincident(g5,g3)
    c: Block(g0)
    c: Block(g5)
FEATURE [Part::Extrusion] Extrude027  label="sideB001"
  Base = -> Sketch036
  Dir = (0,0,1)
  DirMode = 2
  FaceMakerClass = Part::FaceMakerBullseye
  LengthFwd = 3
  LengthRev = 0
  Placement = pos=(0,0,71.7) rot=(0,0,1;0rad)
  Solid = true
  Symmetric = false
FEATURE [Part::MultiFuse] Fusion064  label="removeFromBottom"
  Shapes = -> [Extrude026,Extrude027]
FEATURE [Part::Cut] Cut024  label="bottom009"
  Base = -> Fusion060
  Tool = -> Fusion064
FEATURE [Sketcher::SketchObject] Sketch037  label="topSketch009"
  FullyConstrained = true
  sketch-geometry (6):
    g0: ArcOfCircle CenterX=19 CenterY=19 CenterZ=0 NormalX=0 NormalY=0 NormalZ=1 AngleXU=0 Radius=19 StartAngle=1.5708 EndAngle=3.14159
    g1: LineSegment StartX=5.22862e-06 StartY=19 StartZ=0 EndX=5.22862e-06 EndY=1.19904e-11 EndZ=0
    g2: LineSegment StartX=19 StartY=38 StartZ=0 EndX=124 EndY=38 EndZ=0
    g3: LineSegment StartX=5.22862e-06 StartY=1.19904e-11 StartZ=0 EndX=105 EndY=1.19904e-11 EndZ=0
    g4: ArcOfCircle CenterX=105 CenterY=19 CenterZ=0 NormalX=0 NormalY=0 NormalZ=1 AngleXU=0 Radius=19 StartAngle=4.71239 EndAngle=6.28319
    g5: LineSegment StartX=124 StartY=38 StartZ=0 EndX=124 EndY=19 EndZ=0
  constraints (16):
    c: Block(g0)
    c: Coincident(g1,g0)
    c: Vertical(g1)
    c: Horizontal(g2)
    c: Distance(g2) = 105
    c: Coincident(g2,g0)
    c: Distance(g1) = 19
    c: Coincident(g3,g1)
    c: Horizontal(g3)
    c: Distance(g3) = 105
    c: Block(g4)
    c: Coincident(g4,g3)
    c: Coincident(g5,g2)
    c: Coincident(g5,g4)
    c: Vertical(g5)
    c: Distance(g5) = 19
FEATURE [Part::Extrusion] Extrude028  label="sideB"
  Base = -> Sketch037
  Dir = (0,0,1)
  DirMode = 2
  FaceMakerClass = Part::FaceMakerBullseye
  LengthFwd = 3
  LengthRev = 0
  Placement = pos=(0,0,72) rot=(0,0,1;0rad)
  Solid = true
  Symmetric = false
FEATURE [Sketcher::SketchObject] Sketch038  label="topSketch010"
  FullyConstrained = true
  sketch-geometry (20):
    g0: LineSegment StartX=5.21097e-06 StartY=3 StartZ=0 EndX=5.21097e-06 EndY=19 EndZ=0
    g1: ArcOfCircle CenterX=19 CenterY=19 CenterZ=0 NormalX=0 NormalY=0 NormalZ=1 AngleXU=0 Radius=19 StartAngle=1.5708 EndAngle=3.14159
    g2: ArcOfCircle CenterX=19 CenterY=19 CenterZ=0 NormalX=0 NormalY=0 NormalZ=1 AngleXU=0 Radius=16 StartAngle=1.5708 EndAngle=3.14159
    g3: LineSegment StartX=114 StartY=35 StartZ=0 EndX=19 EndY=35 EndZ=0
    g4: LineSegment StartX=5.21097e-06 StartY=3 StartZ=0 EndX=5.21097e-06 EndY=0 EndZ=0
    g5: LineSegment StartX=3 StartY=0 StartZ=0 EndX=5.21097e-06 EndY=0 EndZ=0
    g6: LineSegment StartX=3 StartY=19 StartZ=0 EndX=3 EndY=0 EndZ=0
    g7: LineSegment StartX=19 StartY=38 StartZ=0 EndX=124 EndY=38 EndZ=0
    g8: Circle CenterX=119 CenterY=35 CenterZ=0 NormalX=0 NormalY=0 NormalZ=1 AngleXU=0 Radius=1
    g9: Circle CenterX=121 CenterY=35 CenterZ=0 NormalX=0 NormalY=0 NormalZ=1 AngleXU=0 Radius=1
    g10: Circle CenterX=121 CenterY=33 CenterZ=0 NormalX=0 NormalY=0 NormalZ=1 AngleXU=0 Radius=1
    g11: BSplineCurve PolesCount=3 KnotsCount=2 Degree=2 IsPeriodic=0
    g12: GeomPoint X=119 Y=35 Z=0
    g13: GeomPoint X=121 Y=33 Z=0
    g14: LineSegment StartX=119 StartY=35 StartZ=0 EndX=114 EndY=35 EndZ=0
    g15: ArcOfCircle CenterX=105 CenterY=19 CenterZ=0 NormalX=0 NormalY=0 NormalZ=1 AngleXU=0 Radius=19 StartAngle=5.7297 EndAngle=6.28319
    g16: ArcOfCircle CenterX=105 CenterY=19 CenterZ=0 NormalX=0 NormalY=0 NormalZ=1 AngleXU=0 Radius=16 StartAngle=5.60905 EndAngle=6.28319
    g17: LineSegment StartX=121 StartY=33 StartZ=0 EndX=121 EndY=19 EndZ=0
    g18: LineSegment StartX=124 StartY=38 StartZ=0 EndX=124 EndY=19 EndZ=0
    g19: LineSegment StartX=117.5 StartY=9.01251 StartZ=0 EndX=121.163 EndY=9.0125 EndZ=0
  constraints (46):
    c: Vertical(g0)
    c: Block(g0)
    c: Coincident(g1,g0)
    c: Block(g1)
    c: Coincident(g2,g1)
    c: Block(g2)
    c: Coincident(g3,g2)
    c: Horizontal(g3)
    c: Tangent(g3,g2)
    c: Coincident(g4,g0)
    c: Distance(g4) = 3
    c: Vertical(g4)
    c: Coincident(g5,g4)
    c: Horizontal(g5)
    c: Coincident(g6,g2)
    c: Coincident(g6,g5)
    c: Vertical(g6)
    c: Horizontal(g7)
    c: Distance(g7) = 105
    c: Coincident(g7,g1)
    c: Block(g3)
    c: Weight(g8) = 1
    c: Equal(g8,g9)
    c: Equal(g8,g10)
    c: InternalAlignment(g8,g11)
    c: InternalAlignment(g9,g11)
    c: InternalAlignment(g10,g11)
    c: InternalAlignment(g12,g11)
    c: InternalAlignment(g13,g11)
    c: Block(g11)
    c: Coincident(g14,g11)
    c: Coincident(g14,g3)
    c: Horizontal(g14)
    c: Block(g15)
    c: Coincident(g16,g15)
    c: Block(g16)
    c: Coincident(g17,g11)
    c: Coincident(g17,g16)
    c: Vertical(g17)
    c: Distance(g17) = 14
    c: Coincident(g18,g7)
    c: Coincident(g18,g15)
    c: Vertical(g18)
    c: Distance(g18) = 19
    c: Coincident(g19,g16)
    c: Coincident(g19,g15)
FEATURE [Part::Extrusion] Extrude029
  Base = -> Sketch038
  Dir = (0,0,1)
  DirMode = 2
  FaceMakerClass = Part::FaceMakerBullseye
  LengthFwd = 72
  LengthRev = 0
  Solid = true
  Symmetric = false
FEATURE [Part::Feature] Face085
  shape: bbox 4.8 x 25.5 x 2e-07 mm, 1 faces, 0 solids (baked)
FEATURE [Part::Revolution] Revolve089  label="moreFrontCaseScrewPost003"
  Angle = 360
  Axis = (0,1,0)
  Base = (0,0,0)
  FaceMakerClass = Part::FaceMakerBullseye
  Placement = pos=(109.5,4.5,3.5) rot=(0,0,1;0rad)
  Solid = false
  Source = -> Face085
  Symmetric = false
FEATURE [Part::Feature] Face086
  shape: bbox 4.8 x 25.5 x 2e-07 mm, 1 faces, 0 solids (baked)
FEATURE [Part::Revolution] Revolve090  label="moreFrontCaseScrewPost004"
  Angle = 360
  Axis = (0,1,0)
  Base = (0,0,0)
  FaceMakerClass = Part::FaceMakerBullseye
  Placement = pos=(109.5,4.5,68.5) rot=(0,0,1;0rad)
  Solid = false
  Source = -> Face086
  Symmetric = false
FEATURE [Part::Fillet] Fillet026
  Base = -> Extrude029
  Edges = 1 edges r=2: [Edge35]
